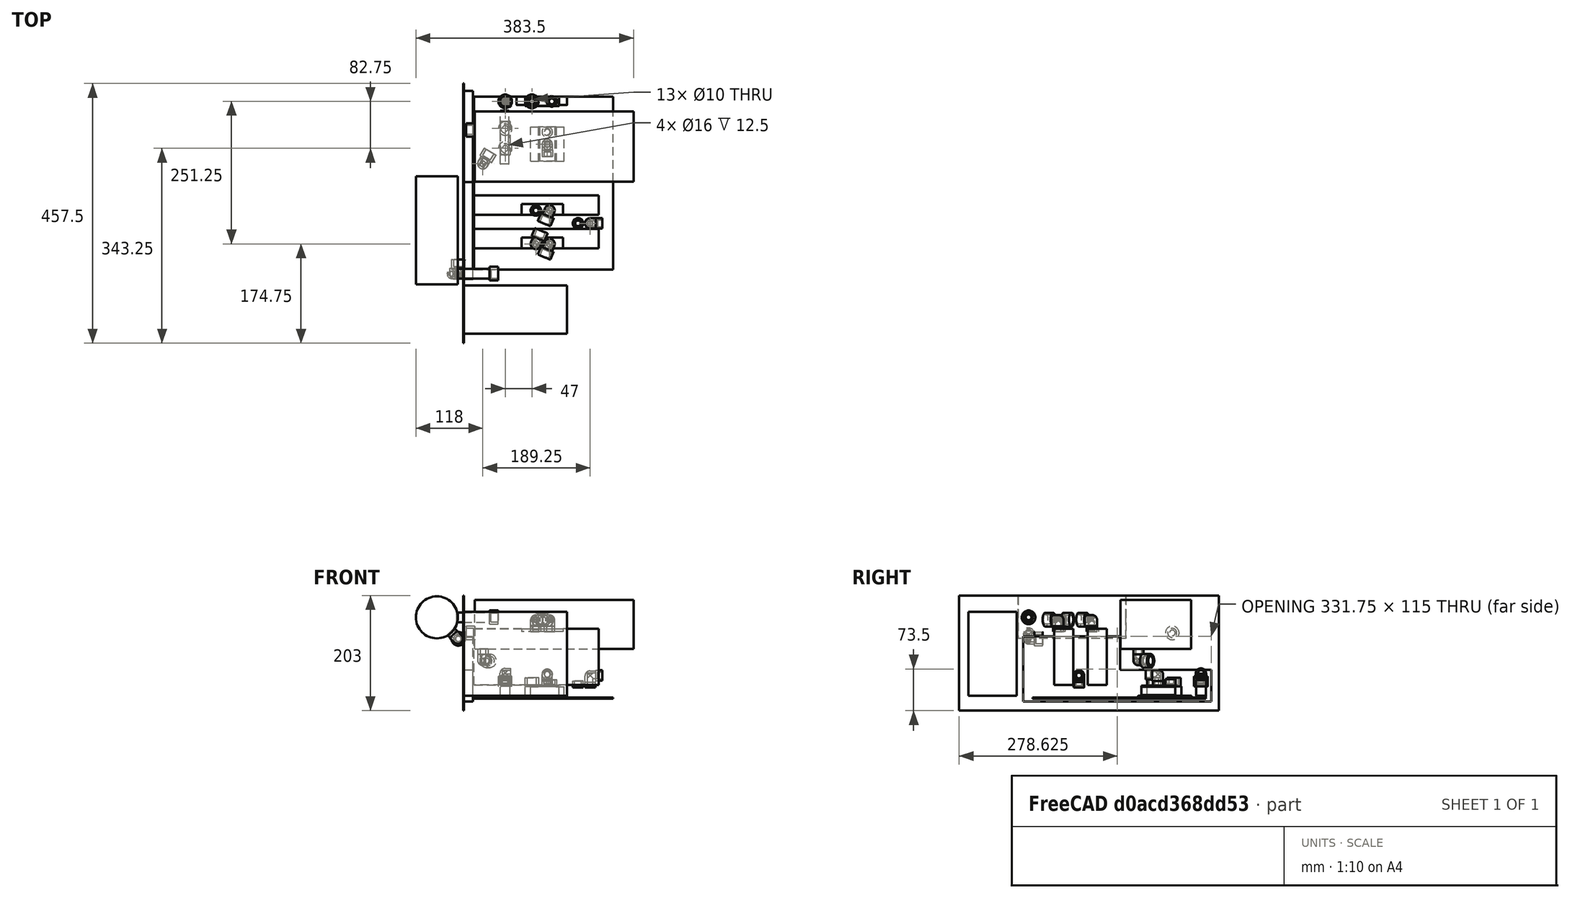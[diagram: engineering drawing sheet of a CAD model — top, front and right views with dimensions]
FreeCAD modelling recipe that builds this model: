
FCSTD DOCUMENT  (FreeCAD 0.18R16131 (Git))
Label: Model
License: All rights reserved
LicenseURL: http://en.wikipedia.org/wiki/All_rights_reserved
objects: TechDraw::DrawViewDimension×43, Part::Part2DObjectPython×40, Part::MultiFuse×29, Sketcher::SketchObject×22, Part::Cylinder×17, Part::Sweep×16, TechDraw::DrawViewPart×16, TechDraw::DrawViewAnnotation×13, Part::Cut×12, Part::Box×12, Part::Extrusion×11, Part::Fillet×7, App::DocumentObjectGroup×7, TechDraw::DrawSVGTemplate×6, TechDraw::DrawPage×6, Spreadsheet::Sheet×1
note: 166 computed .brp shape members not serialized (recipe doc carries the construction recipe); baked Part::Feature solids carry a one-line shape summary decoded from their .brp

FEATURE [Sketcher::SketchObject] Sketch  label="VRMs"
  expr: Constraints[15] = 51mm + References.LargeTubeOuterDiam
  expr: Constraints[7] = References.SmallTubeOuterDiam
  expr: Constraints[1] = References.LargeTubeOuterDiam
  sketch-geometry (11):
    g0: Circle CenterX=47 CenterY=0 CenterZ=0 NormalX=0 NormalY=0 NormalZ=1 AngleXU=0 Radius=8
    g1: Circle CenterX=0 CenterY=-47.7493 CenterZ=0 NormalX=0 NormalY=0 NormalZ=1 AngleXU=0 Radius=8
    g2: LineSegment [constr] StartX=0 StartY=-47.7493 StartZ=0 EndX=0 EndY=-82.7493 EndZ=0
    g3: Circle CenterX=0 CenterY=-82.7493 CenterZ=0 NormalX=0 NormalY=0 NormalZ=1 AngleXU=0 Radius=8
    g4: Circle CenterX=82 CenterY=0 CenterZ=0 NormalX=0 NormalY=0 NormalZ=1 AngleXU=0 Radius=6
    g5: LineSegment [constr] StartX=82 StartY=0 StartZ=0 EndX=74 EndY=0 EndZ=0
    g6: LineSegment [constr] StartX=74 StartY=0 StartZ=0 EndX=74 EndY=-54 EndZ=0
    g7: LineSegment StartX=82 StartY=0 StartZ=0 EndX=74 EndY=-54 EndZ=0
    g8: LineSegment [constr] StartX=47 StartY=0 StartZ=0 EndX=0 EndY=-47.7493 EndZ=0
    g9: LineSegment [constr] StartX=47 StartY=0 StartZ=0 EndX=82 EndY=0 EndZ=0
    g10: LineSegment StartX=47 StartY=0 StartZ=0 EndX=0 EndY=-82.7493 EndZ=0
  constraints (28):
    c: Distance(g-1,g0) = 47
    c: Diameter(g1) = 16
    c: Coincident(g2,g1)
    c: Vertical(g2)
    c: Equal(g0,g1)
    c: Equal(g1,g3)
    c: Coincident(g3,g2)
    c: Diameter(g4) = 12
    c: Horizontal(g5)
    c: Coincident(g4,g5)
    c: Vertical(g6)
    c: Coincident(g5,g6)
    c: Distance(g6) = 54
    c: Coincident(g7,g6)
    c: Coincident(g7,g4)
    c: Distance(g8) = 67
    c: Coincident(g1,g8)
    c: Coincident(g8,g0)
    c: Distance(g0,g4) = 35
    c: Distance(g5,g4) = 8
    c: PointOnObject(g4,g-1)
    c: PointOnObject(g0,g-1)
    c: PointOnObject(g1,g-2)
    c: Coincident(g9,g0)
    c: Coincident(g9,g4)
    c: Equal(g2,g9)
    c: Coincident(g10,g0)
    c: Coincident(g10,g3)
FEATURE [Part::Part2DObjectPython] Circle  label="VRM2-In"  # Draft 2D object (typed FeaturePython)
  FirstAngle = 0
  LastAngle = 0
  MakeFace = true
  Placement = pos=(0,-82.7493,0) rot=(0,0,1;0rad)
  Radius = 8
FEATURE [Part::Part2DObjectPython] Circle001  label="VRM2-Out"  # Draft 2D object (typed FeaturePython)
  FirstAngle = 0
  LastAngle = 0
  MakeFace = true
  Placement = pos=(0,-47.7493,0) rot=(0,0,1;0rad)
  Radius = 8
FEATURE [Part::Part2DObjectPython] Circle002  label="VRM1-Out"  # Draft 2D object (typed FeaturePython)
  FirstAngle = 0
  LastAngle = 0
  MakeFace = true
  Placement = pos=(47,0,0) rot=(0,0,1;0rad)
  Radius = 8
FEATURE [Part::Part2DObjectPython] Circle003  label="VRM1-In"  # Draft 2D object (typed FeaturePython)
  FirstAngle = 0
  LastAngle = 0
  MakeFace = true
  Placement = pos=(82,0,0) rot=(0,0,1;0rad)
  Radius = 6
FEATURE [Sketcher::SketchObject] Sketch001004  label="CPU-Sketch"
  Placement = pos=(0,0,2.5) rot=(0,0,1;0rad)
  expr: Constraints[10] = References.SmallPlugDiam
  expr: Constraints[14] = References.TurnCornLowDiam
  expr: Constraints[7] = References.SmallTubeOuterDiam
  sketch-geometry (7):
    g0: LineSegment [constr] StartX=0 StartY=0 StartZ=0 EndX=74 EndY=0 EndZ=0
    g1: LineSegment [constr] StartX=74 StartY=0 StartZ=0 EndX=74 EndY=-54 EndZ=0
    g2: Circle CenterX=74 CenterY=-54 CenterZ=0 NormalX=0 NormalY=0 NormalZ=1 AngleXU=0 Radius=6
    g3: LineSegment [constr] StartX=74 StartY=-44.75 StartZ=0 EndX=74 EndY=-84.75 EndZ=0
    g4: Circle [constr] CenterX=74 CenterY=-54 CenterZ=0 NormalX=0 NormalY=0 NormalZ=1 AngleXU=0 Radius=9.25
    g5: Circle [constr] CenterX=74 CenterY=-75.75 CenterZ=0 NormalX=0 NormalY=0 NormalZ=1 AngleXU=0 Radius=9
    g6: Circle CenterX=74 CenterY=-75.75 CenterZ=0 NormalX=0 NormalY=0 NormalZ=1 AngleXU=0 Radius=6
  constraints (19):
    c: Distance(g1) = 54
    c: Vertical(g1)
    c: Coincident(g0,g1)
    c: Coincident(g0,g-1)
    c: Horizontal(g0)
    c: Distance(g0) = 74
    c: Coincident(g2,g1)
    c: Diameter(g2) = 12
    c: Vertical(g3)
    c: Coincident(g4,g1)
    c: Diameter(g4) = 18.5
    c: PointOnObject(g3,g4)
    c: PointOnObject(g1,g3)
    c: Distance(g3) = 40
    c: Diameter(g5) = 18
    c: PointOnObject(g5,g3)
    c: PointOnObject(g3,g5)
    c: Coincident(g6,g5)
    c: Equal(g6,g2)
FEATURE [TechDraw::DrawSVGTemplate] Template001
  EditableTexts = Designed_by_Name=Christoph <owner>; Drawing_number=1; FC-Date=Date; FC-SC=1:1; FC-SH=2; FC-Title=PC Water Cooling; Subtitle=CPU - VRM -Tube; Weight=Weight
  Height = 210
  Orientation = 1
  Width = 297
FEATURE [TechDraw::DrawViewAnnotation] Annotation002
  Font = osifont
  LineSpace = 80
  LockPosition = false
  MaxWidth = -1
  Rotation = 0
  ScaleType = 0
  Text = Unbend
  TextSize = 8
  TextStyle = 0
  X = 136.406
  Y = 152.003
FEATURE [TechDraw::DrawViewAnnotation] Annotation003
  Font = osifont
  LineSpace = 80
  LockPosition = false
  MaxWidth = -1
  Rotation = 0
  ScaleType = 0
  Text = Bend
  TextSize = 8
  TextStyle = 0
  X = 108.764
  Y = 89.6129
FEATURE [Sketcher::SketchObject] Sketch001005004  label="GPUs-Base-Sketch"
  expr: Constraints[9] = 68mm + References.SmallPlugHeight
  sketch-geometry (9):
    g0: LineSegment StartX=-55 StartY=-165.75 StartZ=0 EndX=165 EndY=-165.75 EndZ=0
    g1: LineSegment StartX=165 StartY=-165.75 StartZ=0 EndX=165 EndY=-199.75 EndZ=0
    g2: LineSegment StartX=165 StartY=-199.75 StartZ=0 EndX=-55 EndY=-199.75 EndZ=0
    g3: LineSegment StartX=-55 StartY=-199.75 StartZ=0 EndX=-55 EndY=-165.75 EndZ=0
    g4: LineSegment [constr] StartX=74 StartY=-85.75 StartZ=0 EndX=74 EndY=-165.75 EndZ=0
    g5: LineSegment StartX=-55 StartY=-224.75 StartZ=0 EndX=165 EndY=-224.75 EndZ=0
    g6: LineSegment StartX=165 StartY=-258.75 StartZ=0 EndX=-55 EndY=-258.75 EndZ=0
    g7: LineSegment StartX=165 StartY=-224.75 StartZ=0 EndX=165 EndY=-258.75 EndZ=0
    g8: LineSegment StartX=-55 StartY=-258.75 StartZ=0 EndX=-55 EndY=-224.75 EndZ=0
  constraints (28):
    c: DistanceX(g-2,g4) = 74
    c: DistanceY(g-1,g4) = -85.75
    c: Coincident(g1,g2)
    c: Coincident(g2,g3)
    c: Coincident(g3,g0)
    c: Horizontal(g0)
    c: Horizontal(g2)
    c: Vertical(g1)
    c: Vertical(g3)
    c: Distance(g4) = 80
    c: Vertical(g4)
    c: PointOnObject(g4,g0)
    c: Distance(g0) = 220
    c: DistanceX(g-2,g0) = -55
    c: Distance(g1) = 34
    c: Coincident(g5,g7)
    c: Coincident(g7,g6)
    c: Coincident(g6,g8)
    c: Coincident(g8,g5)
    c: Horizontal(g5)
    c: Horizontal(g6)
    c: Vertical(g7)
    c: Vertical(g8)
    c: Equal(g0,g5) = 220
    c: Equal(g1,g7) = 35
    c: PointOnObject(g5,g3)
    c: Distance(g2,g5) = 25
    c: Coincident(g1,g0)
FEATURE [Sketcher::SketchObject] Sketch001005005  label="Chipset-Sketch"
  Placement = pos=(0,0,-1.5) rot=(0,0,1;0rad)
  sketch-geometry (4):
    g0: Circle CenterX=149.75 CenterY=-215 CenterZ=0 NormalX=0 NormalY=0 NormalZ=1 AngleXU=0 Radius=6
    g1: LineSegment [constr] StartX=0 StartY=-215 StartZ=0 EndX=149.75 EndY=-215 EndZ=0
    g2: LineSegment [constr] StartX=149.75 StartY=0 StartZ=0 EndX=149.75 EndY=-215 EndZ=0
    g3: Circle CenterX=128.25 CenterY=-215 CenterZ=0 NormalX=0 NormalY=0 NormalZ=1 AngleXU=0 Radius=6
  constraints (12):
    c: Diameter(g0) = 12
    c: Coincident(g1,g0)
    c: PointOnObject(g1,g-2)
    c: Horizontal(g1)
    c: Vertical(g2)
    c: PointOnObject(g2,g-1)
    c: Coincident(g2,g0)
    c: Distance(g2) = 215
    c: Distance(g1) = 149.75
    c: Equal(g0,g3)
    c: PointOnObject(g3,g1)
    c: Distance(g0,g3) = 21.5
FEATURE [Part::Part2DObjectPython] Circle009  label="CPU-In-Turned"  # Draft 2D object (typed FeaturePython)
  FirstAngle = 0
  LastAngle = 0
  MakeFace = true
  Placement = pos=(74,-88.75,16) rot=(1,0,0;1.5708rad)
  Radius = 6
  expr: Placement.Base.y = -85.75mm - References.SmallPlugOffset
  expr: Placement.Base.z = 1.5mm + References.TurnCornUpZOffset + References.SmallPlugOffset
FEATURE [Part::Part2DObjectPython] Circle010  label="Chipset-In"  # Draft 2D object (typed FeaturePython)
  FirstAngle = 0
  LastAngle = 0
  MakeFace = true
  Placement = pos=(128.25,-215,-1.5) rot=(0,0,1;0rad)
  Radius = 6
FEATURE [Part::Part2DObjectPython] Circle011  label="Chipset-Out"  # Draft 2D object (typed FeaturePython)
  FirstAngle = 0
  LastAngle = 0
  MakeFace = true
  Placement = pos=(149.75,-215,-1.5) rot=(0,0,1;0rad)
  Radius = 6
FEATURE [Sketcher::SketchObject] Sketch001005010  label="Chipset-VRM-Tube-Path3"
  Placement = pos=(0,0,23.5) rot=(0,0,1;0rad)
  expr: Constraints[27] = Constraints.Bend * pi / 4
  expr: Constraints.Bend = 43.5 + 12 / 2
  sketch-geometry (12):
    g0: GeomPoint X=74 Y=-88.75 Z=0
    g1: LineSegment [constr] StartX=0 StartY=-88.75 StartZ=0 EndX=74 EndY=-88.75 EndZ=0
    g2: LineSegment [constr] StartX=74 StartY=-88.75 StartZ=0 EndX=74 EndY=0 EndZ=0
    g3: LineSegment StartX=74 StartY=-88.75 StartZ=0 EndX=74 EndY=-131 EndZ=0
    g4: LineSegment StartX=183 StartY=-155.75 StartZ=0 EndX=98.75 EndY=-155.75 EndZ=0
    g5: ArcOfCircle CenterX=98.75 CenterY=-131 CenterZ=0 NormalX=0 NormalY=0 NormalZ=1 AngleXU=0 Radius=24.75 StartAngle=3.14159 EndAngle=4.71239
    g6: LineSegment [constr] StartX=183 StartY=0 StartZ=0 EndX=183 EndY=-155.75 EndZ=0
    g7: LineSegment [constr] StartX=183 StartY=-155.75 StartZ=0 EndX=0 EndY=-155.75 EndZ=0
    g8: LineSegment StartX=98.75 StartY=-135.75 StartZ=0 EndX=183 EndY=-135.75 EndZ=0
    g9: LineSegment StartX=183 StartY=-135.75 StartZ=0 EndX=221.877 EndY=-135.75 EndZ=0
    g10: LineSegment StartX=221.877 StartY=-135.75 StartZ=0 EndX=264.127 EndY=-135.75 EndZ=0
    g11: LineSegment [constr] StartX=98.75 StartY=-135.75 StartZ=0 EndX=98.75 EndY=-155.75 EndZ=0
  constraints (34):
    c: Coincident(g1,g0)
    c: Coincident(g1,g2)
    c: Horizontal(g1)
    c: Vertical(g2)
    c: PointOnObject(g1,g-2)
    c: PointOnObject(g2,g-1)
    c: Distance(g1) = 74
    c: Distance(g2) = 88.75
    c: Tangent(g5,g3) = -1.5708
    c: Tangent(g5,g4) = 1.5708
    c: Horizontal(g4)
    c: Vertical(g3)
    c: Coincident(g3,g0)
    c: Diameter(g5) = 49.5  'Bend'
    c: Vertical(g6)
    c: Horizontal(g7)
    c: Coincident(g4,g6)
    c: Coincident(g4,g7)
    c: PointOnObject(g6,g-1)
    c: PointOnObject(g7,g-2)
    c: Distance(g6) = 155.75
    c: Distance(g7) = 183
    c: Horizontal(g8)
    c: Horizontal(g9)
    c: Horizontal(g10)
    c: Coincident(g8,g9)
    c: Coincident(g9,g10)
    c: Distance(g9) = 38.8772
    c: Coincident(g11,g4)
    c: Coincident(g11,g8)
    c: Equal(g3,g10)
    c: Vertical(g11)
    c: PointOnObject(g8,g6)
    c: Distance(g11) = 20
FEATURE [Sketcher::SketchObject] Sketch001005011  label="Chipset-VRM-Tube-Path1"
  Placement = pos=(0,0,19.5) rot=(0,0,1;0rad)
  sketch-geometry (4):
    g0: GeomPoint X=162.75 Y=-215 Z=0
    g1: LineSegment [constr] StartX=162.75 StartY=-215 StartZ=0 EndX=0 EndY=-215 EndZ=0
    g2: LineSegment [constr] StartX=162.75 StartY=0 StartZ=0 EndX=162.75 EndY=-215 EndZ=0
    g3: LineSegment StartX=162.75 StartY=-215 StartZ=0 EndX=182.75 EndY=-215 EndZ=0
  constraints (11):
    c: Coincident(g0,g1)
    c: Coincident(g0,g2)
    c: PointOnObject(g1,g-2)
    c: Horizontal(g1)
    c: PointOnObject(g2,g-1)
    c: Vertical(g2)
    c: Distance(g2) = 215
    c: Distance(g1) = 162.75
    c: Horizontal(g3)
    c: Coincident(g3,g0)
    c: Distance(g3) = 20
FEATURE [Part::Part2DObjectPython] Line001  label="Chipset-CPU-Con"  # Draft 2D object (typed FeaturePython)
  ChamferSize = 0
  Closed = false
  End = (182.75,-215,16.5)
  FilletRadius = 0
  Length = 59.3264
  MakeFace = true
  Placement = pos=(183,-155.75,23.5) rot=(-0.578974,-0.576537,0.576537;2.09196rad)
  Points = (2) [(0,4,0),(-59.2505,7,2.84217e-14)]
  Start = (183,-155.75,19.5)
  Subdivisions = 0
  expr: End.z = -1.5mm - References.SmallPlugOffset + References.TurnCornZOffset
  expr: Start.z = 1.5mm - References.SmallPlugOffset + References.TurnCornZOffset
FEATURE [Part::Extrusion] Extrude010  label="Chipset-CPU-Plane"
  Base = -> Line001
  Dir = (-0.999991,0.00421937,-1e-16)
  DirMode = 2
  FaceMakerClass = Part::FaceMakerBullseye
  LengthFwd = 40
  LengthRev = 0
  Reversed = true
  Solid = false
  Symmetric = false
FEATURE [Sketcher::SketchObject] Sketch001005012  label="Chipset-VRM-Tube-Path2"
  ExternalGeometry = -> [Extrude010]
  MapMode = 5
  Placement = pos=(-0.00582736,-1.38108,27.2769) rot=(1,-3e-06,0.000107;3.19218rad)
  Support = -> [Extrude010]
  expr: Constraints[16] = Constraints.Bend * pi / 4
  expr: Constraints.Bend = 43.5 + 12 / 2
  sketch-geometry (7):
    g0: ArcOfCircle CenterX=182.86 CenterY=189.141 CenterZ=0 NormalX=0 NormalY=0 NormalZ=1 AngleXU=0 Radius=24.75 StartAngle=0 EndAngle=1.57501
    g1: ArcOfCircle CenterX=182.902 CenterY=179.273 CenterZ=0 NormalX=0 NormalY=0 NormalZ=1 AngleXU=0 Radius=24.7084 StartAngle=4.7166 EndAngle=6.28319
    g2: LineSegment StartX=207.61 StartY=189.141 StartZ=0 EndX=207.61 EndY=179.273 EndZ=0
    g3: LineSegment [constr] StartX=207.61 StartY=184.207 StartZ=0 EndX=227.61 EndY=184.207 EndZ=0
    g4: LineSegment StartX=227.61 StartY=228.018 StartZ=0 EndX=227.61 EndY=189.141 EndZ=0
    g5: LineSegment StartX=227.61 StartY=179.273 StartZ=0 EndX=227.61 EndY=140.396 EndZ=0
    g6: LineSegment StartX=227.61 StartY=189.141 StartZ=0 EndX=227.61 EndY=179.273 EndZ=0
  constraints (18):
    c: Vertical(g2)
    c: Tangent(g2,g0) = 1.5708
    c: Tangent(g2,g1) = 1.5708
    c: Tangent(g1,g-4) = -1.5708
    c: Tangent(g0,g-3) = 1.5708
    c: Diameter(g0) = 49.5  'Bend'
    c: Vertical(g6)
    c: Vertical(g4)
    c: Vertical(g5)
    c: Horizontal(g3)
    c: Symmetric(g2,g2,g3)
    c: Symmetric(g6,g6,g3)
    c: Equal(g6,g2)
    c: Coincident(g6,g5)
    c: Coincident(g4,g6)
    c: Equal(g5,g4)
    c: Distance(g5) = 38.8772
    c: Distance(g3) = 20
FEATURE [Part::Part2DObjectPython] Circle015  label="Chipset-Corn-Out"  # Draft 2D object (typed FeaturePython)
  FirstAngle = 0
  LastAngle = 0
  MakeFace = true
  Placement = pos=(162.75,-215,16.5) rot=(-0.578974,-0.576537,0.576537;2.09197rad)
  Radius = 6
  expr: Placement.Base.z = -1.5mm - References.SmallPlugOffset + References.TurnCornZOffset
FEATURE [Part::Sweep] Sweep005  label="Chipset-CPU-Tube-1"
  Frenet = false
  Sections = -> [Circle015]
  Solid = false
  Spine = -> Sketch001005011 [Edge1]
  Transition = 1
FEATURE [Part::Part2DObjectPython] Circle016  label="Chipset-CPU-Intermediate-1"  # Draft 2D object (typed FeaturePython)
  FirstAngle = 0
  LastAngle = 0
  MakeFace = true
  Placement = pos=(182.75,-215,16.5) rot=(-0.578974,-0.576537,0.576537;2.09197rad)
  Radius = 6
  expr: Placement.Base.z = -1.5mm + References.TurnCornZOffset - References.SmallPlugOffset
FEATURE [Part::Part2DObjectPython] Circle017  label="Chipset-CPU-Intermediate-2"  # Draft 2D object (typed FeaturePython)
  FirstAngle = 0
  LastAngle = 0
  MakeFace = true
  Placement = pos=(183,-155.75,19.5) rot=(-0.578974,-0.576537,0.576537;2.09197rad)
  Radius = 6
  expr: Placement.Base.z = 1.5mm - References.SmallPlugOffset + References.TurnCornZOffset
FEATURE [Part::Sweep] Sweep006  label="Chipset-CPU-Tube-2"
  Frenet = false
  Sections = -> [Circle016]
  Solid = false
  Spine = -> Sketch001005012 [Edge3,Edge2,Edge1]
  Transition = 1
FEATURE [Part::Sweep] Sweep007  label="Chipset-CPU-Tube-3"
  Frenet = false
  Sections = -> [Circle017]
  Solid = false
  Spine = -> Sketch001005010 [Edge3,Edge2,Edge1]
  Transition = 1
FEATURE [TechDraw::DrawSVGTemplate] Template002
  EditableTexts = Designed_by_Name=Christoph <owner>; Drawing_number=1; FC-Date=Date; FC-SC=1:1; FC-SH=3; FC-Title=PC Water Cooling; Subtitle=Chipset - CPU - Tube; Weight=Weight
  Height = 210
  Orientation = 1
  Width = 297
FEATURE [TechDraw::DrawViewPart] View004  label="Top"
  CoarseView = false
  Direction = (0,0,1)
  Focus = 100
  HardHidden = false
  IsoCount = 0
  IsoHidden = false
  IsoVisible = false
  LockPosition = false
  Perspective = false
  Rotation = 90
  ScaleType = 0
  SeamHidden = false
  SeamVisible = false
  SmoothHidden = false
  SmoothVisible = false
  Source = -> [Sweep005,Sweep006,Sweep007]
  X = 84.2384
  Y = 93.0457
FEATURE [TechDraw::DrawViewPart] View005  label="Side"
  CoarseView = false
  Direction = (0,1,0)
  Focus = 100
  HardHidden = false
  IsoCount = 0
  IsoHidden = false
  IsoVisible = false
  LockPosition = false
  Perspective = false
  Rotation = 0
  ScaleType = 0
  SeamHidden = false
  SeamVisible = false
  SmoothHidden = false
  SmoothVisible = false
  Source = -> [Sweep005,Sweep006,Sweep007]
  X = 193.805
  Y = 79.086
FEATURE [TechDraw::DrawViewDimension] Dimension022
  Arbitrary = false
  FormatSpec = %.2f
  LockPosition = false
  MeasureType = 1
  OverTolerance = 0
  References2D = -> [View005]
  Rotation = 0
  ScaleType = 0
  Type = 2
  UnderTolerance = 0
  X = -27.489
  Y = 18.168
FEATURE [Part::Part2DObjectPython] Circle018  label="Chipset-CPU-Unbend-2-Start"  # Draft 2D object (typed FeaturePython)
  FirstAngle = 0
  LastAngle = 0
  MakeFace = true
  Placement = pos=(227.604,-229.096,18.6236) rot=(-1,0,0;1.5708rad)
  Radius = 6
FEATURE [Part::Sweep] Sweep008  label="Chipset-CPU-Unbend-2"
  Frenet = false
  Sections = -> [Circle018]
  Solid = false
  Spine = -> Sketch001005012 [Edge4,Edge5,Edge6]
  Transition = 1
FEATURE [Part::Part2DObjectPython] Circle019  label="Chipset-CPU-Unbend-3-Start"  # Draft 2D object (typed FeaturePython)
  FirstAngle = 0
  LastAngle = 0
  MakeFace = true
  Placement = pos=(114.75,-135.75,23.5) rot=(0.57735,0.57735,0.57735;2.0944rad)
  Radius = 6
FEATURE [Part::Sweep] Sweep009  label="Chipset-CPU-Unbend-3"
  Frenet = false
  Sections = -> [Circle019]
  Solid = false
  Spine = -> Sketch001005010 [Edge4,Edge5,Edge6]
  Transition = 1
FEATURE [TechDraw::DrawViewPart] View006  label="Unbend1"
  CoarseView = false
  Direction = (0,1,0)
  Focus = 100
  HardHidden = false
  IsoCount = 0
  IsoHidden = false
  IsoVisible = false
  LockPosition = false
  Perspective = false
  Rotation = 0
  ScaleType = 0
  SeamHidden = false
  SeamVisible = false
  SmoothHidden = false
  SmoothVisible = false
  Source = -> [Sweep005]
  X = 272.886
  Y = 190.725
FEATURE [TechDraw::DrawViewPart] View007  label="Unbend2"
  CoarseView = false
  Direction = (1,0,0)
  Focus = 100
  HardHidden = false
  IsoCount = 0
  IsoHidden = false
  IsoVisible = false
  LockPosition = false
  Perspective = false
  Rotation = 0
  ScaleType = 0
  SeamHidden = false
  SeamVisible = false
  SmoothHidden = false
  SmoothVisible = false
  Source = -> [Sweep008]
  X = 219.254
  Y = 187.598
FEATURE [TechDraw::DrawViewPart] View008  label="Unbend3"
  CoarseView = false
  Direction = (0,1,0)
  Focus = 100
  HardHidden = false
  IsoCount = 0
  IsoHidden = false
  IsoVisible = false
  LockPosition = false
  Perspective = false
  Rotation = 0
  ScaleType = 0
  SeamHidden = false
  SeamVisible = false
  SmoothHidden = false
  SmoothVisible = false
  Source = -> [Sweep009]
  X = 93.7486
  Y = 184.77
FEATURE [TechDraw::DrawViewDimension] Dimension027
  Arbitrary = false
  FormatSpec = %.2f
  LockPosition = false
  MeasureType = 1
  OverTolerance = 0
  References2D = -> [View008]
  Rotation = 0
  ScaleType = 0
  Type = 1
  UnderTolerance = 0
  X = 0.425571
  Y = -9.8662
FEATURE [TechDraw::DrawViewDimension] Dimension028
  Arbitrary = false
  FormatSpec = %.2f
  LockPosition = false
  MeasureType = 1
  OverTolerance = 0
  References2D = -> [View007]
  Rotation = 0
  ScaleType = 0
  Type = 0
  UnderTolerance = 0
  X = 3.46058
  Y = -10.0125
FEATURE [TechDraw::DrawViewDimension] Dimension029
  Arbitrary = false
  FormatSpec = %.2f
  LockPosition = false
  MeasureType = 1
  OverTolerance = 0
  References2D = -> [View006]
  Rotation = 0
  ScaleType = 0
  Type = 1
  UnderTolerance = 0
  X = -0.341951
  Y = -24.0175
FEATURE [TechDraw::DrawViewAnnotation] Annotation004
  Font = osifont
  LineSpace = 80
  LockPosition = false
  MaxWidth = -1
  Rotation = 0
  ScaleType = 0
  Text = Top View
  TextSize = 8
  TextStyle = 0
  X = 49.8933
  Y = 147.612
FEATURE [TechDraw::DrawViewAnnotation] Annotation005
  Font = osifont
  LineSpace = 80
  LockPosition = false
  MaxWidth = -1
  Rotation = 0
  ScaleType = 0
  Text = Side View
  TextSize = 8
  TextStyle = 0
  X = 213.956
  Y = 102.638
FEATURE [TechDraw::DrawViewAnnotation] Annotation006
  Font = osifont
  LineSpace = 80
  LockPosition = false
  MaxWidth = -1
  Rotation = 0
  ScaleType = 0
  Text = Unbend
  TextSize = 8
  TextStyle = 0
  X = 232.772
  Y = 161.972
FEATURE [Spreadsheet::Sheet] Spreadsheet  label="References"
  cells = B2=Small Plug; C2=Large Plug; D2=Extension; A3=Diameter; B3(SmallPlugDiam)==18.5mm; C3(LargePlugDiam)==24mm; D3(ExtensionDiamater)==17mm; A4=Height; B4(SmallPlugHeight)==12mm; C4(LargePlugHeight)==15mm; D4(ExtensionHeight)==7mm; A5=Tube Offset; B5(SmallPlugOffset)==3mm; C5(LargePlugOffset)==LargePlugHeight - 12.5mm; B7=SmallTube; C7=LargeTube; A8=Inner Diameter; B8(SmallTubeInnerDiam)==10mm; C8(LargeTubeInnerDiam)==13mm; A9=Outer Diameter; B9(SmallTubeOuterDiam)==12mm; C9(LargeTubeOuterDiam)==16mm; A10=Radius; B10(SmallTubeBendDiam)==43.5mm + SmallTubeOuterDiam; C10(LargeTubeBendDiam)==45mm + LargeTubeOuterDiam; A11=Straight Length; B11(SmallTubeStraightLen)==10mm; C11(LargTubeStraightLen)==20mm; B13=TurnableCorner; C13=Corner; A14=Height Offset; B14(TurnCornZOffset)==TurnCornLowHeight + TurnCornUpZOffset; C14(CornZOffset)==TurnCornUpZOffset; A15=Front Offset; B15(TurnCornXOffset)==TurnCornUpLen - TurnCornLowDiam / 2; C15(CornXOffset)==TurnCornXOffset; A16=Lower Diam; B16(TurnCornLowDiam)==18mm; C16==0mm; A17=Upper Width; B17(TurnCornUpWid)==18mm; C17(CornWid)==TurnCornUpWid; A18=Upper Length; B18(TurnCornUpLen)==19mm; C18(CornLen)==TurnCornUpLen; A19=Upper Height Offset; B19(TurnCornUpZOffset)==TurnCornUpHeight - 2mm - SmallTubeOuterDiam / 2; C19==TurnCornUpZOffset; A20=Lower Height; B20(TurnCornLowHeight)==9.5mm; C20==0mm; A21=Upper Height; B21(TurnCornUpHeight)==19.5mm; C21(CornHeight)==TurnCornUpHeight; A24=Unbend Tube Offset; B24(UnbendOffset)==20mm
FEATURE [Part::Part2DObjectPython] Line004  label="VRM-VRM-Con"  # Draft 2D object (typed FeaturePython)
  ChamferSize = 0
  Closed = false
  End = (0,-47.7493,0)
  FilletRadius = 0
  Length = 67
  MakeFace = true
  Points = (2) [(47,0,0),(0,-47.7493,0)]
  Start = (47,0,0)
  Subdivisions = 0
FEATURE [Part::Part2DObjectPython] Circle022  label="CPU-In"  # Draft 2D object (typed FeaturePython)
  FirstAngle = 0
  LastAngle = 0
  MakeFace = true
  Placement = pos=(74,-75.75,2.5) rot=(0,0,1;0rad)
  Radius = 6
FEATURE [Part::Part2DObjectPython] Circle023  label="CPU-Out"  # Draft 2D object (typed FeaturePython)
  FirstAngle = 0
  LastAngle = 0
  MakeFace = true
  Placement = pos=(74,-54,1.5) rot=(0,0,1;0rad)
  Radius = 6
FEATURE [Part::Part2DObjectPython] Line005  label="CPU-VRM-Con"  # Draft 2D object (typed FeaturePython)
  ChamferSize = 0
  Closed = false
  End = (74,-54,0)
  FilletRadius = 0
  Length = 54.5894
  MakeFace = true
  Points = (2) [(82,0,0),(74,-54,0)]
  Start = (82,0,0)
  Subdivisions = 0
FEATURE [Part::Extrusion] Extrude011  label="CPU-VRM-Plane"
  Base = -> Line005
  Dir = (0,0,1)
  DirMode = 2
  FaceMakerClass = Part::FaceMakerBullseye
  LengthFwd = 60
  LengthRev = 0
  Solid = false
  Symmetric = false
FEATURE [Sketcher::SketchObject] Sketch001005014  label="CPU-VRM-Sketch"
  ExternalGeometry = -> [Extrude011]
  MapMode = 5
  Placement = pos=(80.2389,-11.8872,0) rot=(0.633886,0.546895,0.546895;2.01166rad)
  Support = -> [Extrude011]
  expr: Constraints[12] = References.UnbendOffset
  expr: Constraints[2] = References.SmallTubeStraightLen
  sketch-geometry (9):
    g0: LineSegment StartX=-42.5724 StartY=2 StartZ=0 EndX=-42.5724 EndY=12 EndZ=0
    g1: ArcOfCircle CenterX=-15.2824 CenterY=12 CenterZ=0 NormalX=0 NormalY=0 NormalZ=1 AngleXU=0 Radius=27.29 StartAngle=1.5708 EndAngle=3.14159
    g2: LineSegment StartX=-15.2824 StartY=39.29 StartZ=0 EndX=-15.273 EndY=39.29 EndZ=0
    g3: ArcOfCircle CenterX=-15.273 CenterY=12 CenterZ=0 NormalX=0 NormalY=0 NormalZ=1 AngleXU=0 Radius=27.29 StartAngle=0 EndAngle=1.5708
    g4: LineSegment StartX=-15.273 StartY=59.29 StartZ=0 EndX=-15.2824 EndY=59.29 EndZ=0
    g5: LineSegment StartX=-15.273 StartY=59.29 StartZ=0 EndX=39.0705 EndY=59.29 EndZ=0
    g6: LineSegment StartX=-15.2824 StartY=59.29 StartZ=0 EndX=-68.1259 EndY=59.29 EndZ=0
    g7: LineSegment [constr] StartX=-15.2777 StartY=59.29 StartZ=0 EndX=-15.2777 EndY=39.29 EndZ=0
    g8: LineSegment StartX=12.017 StartY=12 StartZ=0 EndX=12.017 EndY=0.5 EndZ=0
  constraints (25):
    c: Tangent(g0,g1) = 1.5708
    c: Tangent(g0,g-4) = -1.5708
    c: Distance(g0) = 10
    c: Tangent(g2,g1) = 1.5708
    c: Tangent(g3,g2) = 1.5708
    c: Horizontal(g2)
    c: Equal(g3,g1)
    c: Equal(g2,g4)
    c: Horizontal(g4)
    c: Symmetric(g4,g4,g7)
    c: Vertical(g7)
    c: Symmetric(g2,g2,g7)
    c: Distance(g7) = 20
    c: Distance(g5) = 54.3435
    c: Distance(g6) = 52.8435
    c: Coincident(g4,g6)
    c: Coincident(g5,g4)
    c: Horizontal(g5)
    c: Horizontal(g6)
    c: Distance(g0,g-4) = 2
    c: Vertical(g8)
    c: Distance(g8,g-3) = 0.5
    c: Tangent(g8,g3) = 1.5708
    c: PointOnObject(g8,g-3)
    c: Diameter(g1) = 54.58
FEATURE [Part::Part2DObjectPython] Circle024  label="CPU-VRM-Unbend-Start"  # Draft 2D object (typed FeaturePython)
  FirstAngle = 0
  LastAngle = 0
  MakeFace = true
  Placement = pos=(70.253,-79.2924,59.775) rot=(0.994616,-0.073275,-0.073275;1.5762rad)
  Radius = 6
FEATURE [Part::Sweep] Sweep  label="CPU-VRM-Unbend"
  Frenet = false
  Sections = -> [Circle024]
  Solid = false
  Spine = -> Sketch001005014 [Edge8,Edge7,Edge6]
  Transition = 1
FEATURE [TechDraw::DrawViewPart] View002  label="Unbend"
  CoarseView = false
  Direction = (0.54,-0.08,0)
  Focus = 100
  HardHidden = false
  IsoCount = 0
  IsoHidden = false
  IsoVisible = false
  LockPosition = false
  Perspective = false
  Rotation = 0
  ScaleType = 0
  SeamHidden = false
  SeamVisible = false
  SmoothHidden = false
  SmoothVisible = false
  Source = -> [Sweep]
  X = 138.605
  Y = 177.84
FEATURE [TechDraw::DrawViewDimension] Dimension035
  Arbitrary = false
  FormatSpec = %.2f
  LockPosition = false
  MeasureType = 1
  OverTolerance = 0
  References2D = -> [View002]
  Rotation = 0
  ScaleType = 0
  Type = 1
  UnderTolerance = 0
  X = -0.301104
  Y = -13.2265
FEATURE [Part::Sweep] Sweep014  label="CPU-VRM-Tube"
  Frenet = false
  Sections = -> [Circle023]
  Solid = false
  Spine = -> Sketch001005014 [Edge1,Edge2,Edge3,Edge4,Edge5]
  Transition = 1
FEATURE [TechDraw::DrawViewPart] View003  label="Side001"
  CoarseView = false
  Direction = (-54,8,0)
  Focus = 100
  HardHidden = false
  IsoCount = 0
  IsoHidden = false
  IsoVisible = false
  LockPosition = false
  Perspective = false
  Rotation = 0
  ScaleType = 0
  SeamHidden = false
  SeamVisible = false
  SmoothHidden = false
  SmoothVisible = false
  Source = -> [Sweep014]
  X = 88.8407
  Y = 48.4082
FEATURE [TechDraw::DrawViewDimension] Dimension047
  Arbitrary = false
  FormatSpec = %.2f
  LockPosition = false
  MeasureType = 1
  OverTolerance = 0
  References2D = -> [View004]
  Rotation = 0
  ScaleType = 0
  Type = 1
  UnderTolerance = 0
  X = -26.3419
  Y = -48.8146
FEATURE [TechDraw::DrawViewDimension] Dimension054
  Arbitrary = false
  FormatSpec = %.2f
  LockPosition = false
  MeasureType = 1
  OverTolerance = 0
  References2D = -> [View005]
  Rotation = 0
  ScaleType = 0
  Type = 2
  UnderTolerance = 0
  X = 77.308
  Y = 2.11203
FEATURE [TechDraw::DrawViewDimension] Dimension055
  Arbitrary = false
  FormatSpec = %.2f
  LockPosition = false
  MeasureType = 1
  OverTolerance = 0
  References2D = -> [View004]
  Rotation = 0
  ScaleType = 0
  Type = 2
  UnderTolerance = 0
  X = -11.4999
  Y = 24.5166
FEATURE [TechDraw::DrawViewDimension] Dimension056
  Arbitrary = false
  FormatSpec = %.2f
  LockPosition = false
  MeasureType = 1
  OverTolerance = 0
  References2D = -> [View004]
  Rotation = 0
  ScaleType = 0
  Type = 2
  UnderTolerance = 0
  X = -45.683
  Y = -30.4883
FEATURE [TechDraw::DrawViewDimension] Dimension057
  Arbitrary = false
  FormatSpec = %.2f
  LockPosition = false
  MeasureType = 1
  OverTolerance = 0
  References2D = -> [View004]
  Rotation = 0
  ScaleType = 0
  Type = 2
  UnderTolerance = 0
  X = 13.3488
  Y = 1.82286
FEATURE [TechDraw::DrawViewDimension] Dimension058
  Arbitrary = false
  FormatSpec = %.2f
  LockPosition = false
  MeasureType = 1
  OverTolerance = 0
  References2D = -> [View004]
  Rotation = 0
  ScaleType = 0
  Type = 1
  UnderTolerance = 0
  X = 43.1032
  Y = 56.7834
FEATURE [TechDraw::DrawViewDimension] Dimension059
  Arbitrary = false
  FormatSpec = %.2f
  LockPosition = false
  MeasureType = 1
  OverTolerance = 0
  References2D = -> [View004]
  Rotation = 0
  ScaleType = 0
  Type = 1
  UnderTolerance = 0
  X = -30.1279
  Y = -75.7031
FEATURE [TechDraw::DrawViewDimension] Dimension060
  Arbitrary = false
  FormatSpec = %.2f
  LockPosition = false
  MeasureType = 1
  OverTolerance = 0
  References2D = -> [View004]
  Rotation = 0
  ScaleType = 0
  Type = 1
  UnderTolerance = 0
  X = 30.2026
  Y = 32.8589
FEATURE [TechDraw::DrawViewDimension] Dimension061
  Arbitrary = false
  FormatSpec = %.2f
  LockPosition = false
  MeasureType = 1
  OverTolerance = 0
  References2D = -> [View004]
  Rotation = 0
  ScaleType = 0
  Type = 2
  UnderTolerance = 0
  X = -63.6273
  Y = 34.9692
FEATURE [TechDraw::DrawPage] Page002  label="Chipset-CPU-Tube-Drawing"
  KeepUpdated = true
  ProjectionType = 0
  Template = -> Template002
  Views = -> [View004,View005,Dimension022,View006,View007,View008,Dimension027,Dimension028,Dimension029,Annotation004,Annotation005,Annotation006,Dimension047,Dimension054,Dimension055,Dimension056,Dimension057,Dimension058,Dimension059,Dimension060,Dimension061]
FEATURE [Part::Extrusion] Extrude012  label="GPU-Base"
  Base = -> Sketch001005004
  Dir = (0,0,1)
  DirMode = 2
  FaceMakerClass = Part::FaceMakerBullseye
  LengthFwd = 99
  LengthRev = 0
  Solid = true
  Symmetric = false
FEATURE [Sketcher::SketchObject] Sketch001005015  label="GPU-Pocket-Sketch"
  ExternalGeometry = -> [Extrude012]
  MapMode = 45
  Placement = pos=(55,-212.25,99) rot=(0,0,1;1.5708rad)
  Support = -> [Extrude012]
  sketch-geometry (10):
    g0: LineSegment [constr] StartX=12.5 StartY=110 StartZ=0 EndX=12.5 EndY=26 EndZ=0
    g1: LineSegment StartX=12.5 StartY=26 StartZ=0 EndX=31.5 EndY=26 EndZ=0
    g2: LineSegment StartX=31.5 StartY=26 StartZ=0 EndX=31.5 EndY=-47 EndZ=0
    g3: LineSegment StartX=12.5 StartY=26 StartZ=0 EndX=12.5 EndY=-47 EndZ=0
    g4: LineSegment StartX=12.5 StartY=-47 StartZ=0 EndX=31.5 EndY=-47 EndZ=0
    g5: LineSegment [constr] StartX=-46.5 StartY=110 StartZ=0 EndX=-46.5 EndY=26 EndZ=0
    g6: LineSegment StartX=-46.5 StartY=26 StartZ=0 EndX=-27.5 EndY=26 EndZ=0
    g7: LineSegment StartX=-27.5 StartY=26 StartZ=0 EndX=-27.5 EndY=-47 EndZ=0
    g8: LineSegment StartX=-27.5 StartY=-47 StartZ=0 EndX=-46.5 EndY=-47 EndZ=0
    g9: LineSegment StartX=-46.5 StartY=-47 StartZ=0 EndX=-46.5 EndY=26 EndZ=0
  constraints (28):
    c: Coincident(g0,g1)
    c: Coincident(g1,g2)
    c: Vertical(g0)
    c: Horizontal(g1)
    c: Vertical(g2)
    c: Coincident(g0,g-3)
    c: Distance(g0) = 84
    c: Distance(g1) = 19
    c: Distance(g2) = 73
    c: Coincident(g4,g2)
    c: Coincident(g4,g3)
    c: Coincident(g0,g3)
    c: Horizontal(g4)
    c: Vertical(g3)
    c: Coincident(g6,g7)
    c: Coincident(g7,g8)
    c: Coincident(g8,g9)
    c: Coincident(g9,g6)
    c: Horizontal(g6)
    c: Horizontal(g8)
    c: Vertical(g7)
    c: Vertical(g9)
    c: Coincident(g6,g5)
    c: Coincident(g5,g-4)
    c: Vertical(g5)
    c: Equal(g6,g1)
    c: Equal(g5,g0)
    c: Equal(g2,g7)
FEATURE [Part::Extrusion] Extrude013  label="Con-Holes"
  Base = -> Sketch001005015
  Dir = (0,0,1)
  DirMode = 2
  FaceMakerClass = Part::FaceMakerBullseye
  LengthFwd = 5
  LengthRev = 0
  Reversed = true
  Solid = true
  Symmetric = false
FEATURE [Part::Cut] Cut002  label="GPUs"
  Base = -> Extrude012
  Tool = -> Extrude013
FEATURE [Sketcher::SketchObject] Sketch001005016  label="GPU-Sketch"
  ExternalGeometry = -> [Cut002]
  MapMode = 45
  Placement = pos=(65.5,-219.75,94) rot=(0,0,1;0rad)
  Support = -> [Cut002]
  expr: Constraints[32] = Constraints.Right
  expr: Constraints[17] = References.LargeTubeOuterDiam
  expr: Constraints[33] = Constraints.Left
  expr: Constraints[15] = References.SmallTubeOuterDiam
  expr: Constraints[0] = References.TurnCornLowDiam
  sketch-geometry (17):
    g0: Circle [constr] CenterX=12.5 CenterY=27.5 CenterZ=0 NormalX=0 NormalY=0 NormalZ=1 AngleXU=0 Radius=9
    g1: GeomPoint X=3.5 Y=27.5 Z=0
    g2: Circle [constr] CenterX=-11.5 CenterY=27.5 CenterZ=0 NormalX=0 NormalY=0 NormalZ=1 AngleXU=0 Radius=9
    g3: LineSegment [constr] StartX=-11.5 StartY=27.5 StartZ=0 EndX=12.5 EndY=27.5 EndZ=0
    g4: GeomPoint X=-2.5 Y=27.5 Z=0
    g5: LineSegment [constr] StartX=-11.5 StartY=39 StartZ=0 EndX=-11.5 EndY=36.5 EndZ=0
    g6: Circle CenterX=-11.5 CenterY=27.5 CenterZ=0 NormalX=0 NormalY=0 NormalZ=1 AngleXU=0 Radius=6
    g7: Circle CenterX=12.5 CenterY=27.5 CenterZ=0 NormalX=0 NormalY=0 NormalZ=1 AngleXU=0 Radius=8
    g8: Circle CenterX=-11.5 CenterY=-31.5 CenterZ=0 NormalX=0 NormalY=0 NormalZ=1 AngleXU=0 Radius=8
    g9: Circle [constr] CenterX=-11.5 CenterY=-31.5 CenterZ=0 NormalX=0 NormalY=0 NormalZ=1 AngleXU=0 Radius=9
    g10: Circle [constr] CenterX=12.5 CenterY=-31.5 CenterZ=0 NormalX=0 NormalY=0 NormalZ=1 AngleXU=0 Radius=9
    g11: Circle CenterX=12.5 CenterY=-31.5 CenterZ=0 NormalX=0 NormalY=0 NormalZ=1 AngleXU=0 Radius=8
    g12: LineSegment [constr] StartX=-11.5 StartY=-31.5 StartZ=0 EndX=12.5 EndY=-31.5 EndZ=0
    g13: GeomPoint X=-2.5 Y=-31.5 Z=0
    g14: GeomPoint X=3.5 Y=-31.5 Z=0
    g15: LineSegment [constr] StartX=-11.5 StartY=-20 StartZ=0 EndX=-11.5 EndY=-22.5 EndZ=0
    g16: LineSegment StartX=12.5 StartY=27.5 StartZ=0 EndX=-11.5 EndY=-31.5 EndZ=0
  constraints (40):
    c: Diameter(g0) = 18
    c: PointOnObject(g1,g0)
    c: Distance(g1,g-3) = 40  'Left'
    c: Equal(g2,g0)
    c: Coincident(g3,g0)
    c: Coincident(g2,g3)
    c: Horizontal(g3)
    c: PointOnObject(g4,g2)
    c: Distance(g4,g-5) = 39  'Right'
    c: PointOnObject(g4,g3)
    c: PointOnObject(g1,g3)
    c: Distance(g5) = 2.5
    c: Perpendicular(g5,g-6) = 1.5708
    c: PointOnObject(g5,g2)
    c: PointOnObject(g2,g5)
    c: Diameter(g6) = 12
    c: Coincident(g6,g2)
    c: Diameter(g7) = 16
    c: Coincident(g7,g0)
    c: Coincident(g9,g8)
    c: Coincident(g9,g12)
    c: Coincident(g11,g10)
    c: Coincident(g11,g12)
    c: Horizontal(g12)
    c: Equal(g9,g2)
    c: Equal(g8,g7)
    c: Equal(g11,g7)
    c: Equal(g10,g0)
    c: PointOnObject(g13,g12)
    c: PointOnObject(g13,g9)
    c: PointOnObject(g14,g10)
    c: PointOnObject(g14,g12)
    c: Distance(g13,g-8) = 39
    c: Distance(g14,g-4) = 40
    c: Perpendicular(g15,g-7) = 1.5708
    c: PointOnObject(g15,g9)
    c: PointOnObject(g8,g15)
    c: Equal(g15,g5)
    c: Coincident(g16,g7)
    c: Coincident(g16,g8)
FEATURE [Part::Part2DObjectPython] Circle025  label="GPU2-Out"  # Draft 2D object (typed FeaturePython)
  FirstAngle = 0
  LastAngle = 0
  MakeFace = true
  Placement = pos=(54,-192.25,97) rot=(0,0,1;0rad)
  Radius = 6
FEATURE [Part::Part2DObjectPython] Circle026  label="GPU1-Out"  # Draft 2D object (typed FeaturePython)
  FirstAngle = 0
  LastAngle = 0
  MakeFace = true
  Placement = pos=(54,-251.25,94) rot=(0,0,1;0rad)
  Radius = 8
FEATURE [Part::Part2DObjectPython] Circle027  label="GPU1-In"  # Draft 2D object (typed FeaturePython)
  FirstAngle = 0
  LastAngle = 0
  MakeFace = true
  Placement = pos=(78,-251.25,94) rot=(0,0,1;0rad)
  Radius = 8
FEATURE [Part::Part2DObjectPython] Circle028  label="GPU2-In"  # Draft 2D object (typed FeaturePython)
  FirstAngle = 0
  LastAngle = 0
  MakeFace = true
  Placement = pos=(78,-192.25,94) rot=(0,0,1;0rad)
  Radius = 8
FEATURE [Part::Part2DObjectPython] Line  label="CPU-Chipset-Con"  # Draft 2D object (typed FeaturePython)
  ChamferSize = 0
  Closed = false
  End = (128.25,-215,-1.5)
  FilletRadius = 0
  Length = 77.6571
  MakeFace = false
  Placement = pos=(64,-164,0) rot=(0,0,1;0rad)
  Points = (2) [(-10,-28.25,-1.5),(64.25,-51,-1.5)]
  Start = (54,-192.25,-1.5)
  Subdivisions = 0
  Support = -> [Circle025]
FEATURE [Part::Extrusion] Extrude014  label="GPU-Chipset-Plane"
  Base = -> Line
  Dir = (0,0,1)
  DirMode = 2
  FaceMakerClass = Part::FaceMakerBullseye
  LengthFwd = 120
  LengthRev = 0
  Solid = false
  Symmetric = false
FEATURE [Sketcher::SketchObject] Sketch001005017  label="GPU-Chipset-Sketch"
  ExternalGeometry = -> [Extrude014]
  MapMode = 5
  Placement = pos=(-49.2151,-160.625,0) rot=(0.105309,0.703175,0.703175;2.93175rad)
  Support = -> [Extrude014]
  expr: Constraints[15] = References.SmallTubeBendDiam * pi / 4 + References.SmallTubeStraightLen
  expr: Constraints[9] = References.SmallTubeStraightLen
  expr: Constraints[14] = References.UnbendOffset
  expr: Constraints[10] = References.SmallTubeBendDiam
  expr: Constraints[16] = References.SmallTubeBendDiam * pi / 4 + Constraints.GPUZOffset + References.SmallTubeStraightLen
  sketch-geometry (9):
    g0: LineSegment StartX=-185.608 StartY=-1.5 StartZ=0 EndX=-185.608 EndY=107 EndZ=0
    g1: LineSegment StartX=-107.951 StartY=97 StartZ=0 EndX=-107.951 EndY=107 EndZ=0
    g2: ArcOfCircle CenterX=-135.701 CenterY=107 CenterZ=0 NormalX=0 NormalY=0 NormalZ=1 AngleXU=0 Radius=27.75 StartAngle=2e-16 EndAngle=1.5708
    g3: ArcOfCircle CenterX=-157.858 CenterY=107 CenterZ=0 NormalX=0 NormalY=0 NormalZ=1 AngleXU=0 Radius=27.75 StartAngle=1.5708 EndAngle=3.14159
    g4: LineSegment StartX=-135.701 StartY=134.75 StartZ=0 EndX=-157.858 EndY=134.75 EndZ=0
    g5: LineSegment [constr] StartX=-146.78 StartY=134.75 StartZ=0 EndX=-146.78 EndY=154.75 EndZ=0
    g6: LineSegment StartX=-135.701 StartY=154.75 StartZ=0 EndX=-82.1117 EndY=154.75 EndZ=0
    g7: LineSegment StartX=-157.858 StartY=154.75 StartZ=0 EndX=-309.948 EndY=154.75 EndZ=0
    g8: LineSegment StartX=-157.858 StartY=154.75 StartZ=0 EndX=-135.701 EndY=154.75 EndZ=0
  constraints (23):
    c: Tangent(g4,g2) = -1.5708
    c: Tangent(g2,g1) = -1.5708
    c: Tangent(g4,g3) = -1.5708
    c: Tangent(g3,g0) = 1.5708
    c: Tangent(g0,g-4) = -1.5708
    c: Tangent(g1,g-3) = -1.5708
    c: Horizontal(g4)
    c: Equal(g2,g3)
    c: Distance(g1,g-3) = 98.5  'GPUZOffset'
    c: Distance(g1) = 10
    c: Diameter(g2) = 55.5
    c: Symmetric(g6,g7,g5)
    c: Symmetric(g4,g4,g5)
    c: Vertical(g5)
    c: Distance(g5) = 20
    c: Distance(g6) = 53.5896
    c: Distance(g7) = 152.09
    c: Horizontal(g7)
    c: Horizontal(g6)
    c: Coincident(g8,g7)
    c: Coincident(g8,g6)
    c: Horizontal(g8)
    c: Equal(g8,g4)
FEATURE [Part::Part2DObjectPython] Circle029  label="GPU-Chipset-Unbend-Start"  # Draft 2D object (typed FeaturePython)
  FirstAngle = 0
  LastAngle = 0
  MakeFace = true
  Placement = pos=(29.2941,-184.68,151.75) rot=(-0.691105,-0.511065,0.511065;1.93213rad)
  Radius = 6
  expr: Radius = References.SmallTubeOuterDiam / 2
FEATURE [Part::Sweep] Sweep015  label="GPU-Chipset-Unbend"
  Frenet = false
  Sections = -> [Circle029]
  Solid = false
  Spine = -> Sketch001005017 [Edge8,Edge7,Edge6]
  Transition = 1
FEATURE [Part::Sweep] Sweep016  label="GPU-Chipset-Tube"
  Frenet = false
  Sections = -> [Circle025]
  Solid = false
  Spine = -> Sketch001005017 [Edge5,Edge4,Edge3,Edge2,Edge1]
  Transition = 1
FEATURE [Part::Cylinder] Cylinder019  label="LargePlugBase"
  Angle = 360
  AttacherType = Attacher::AttachEngine3D
  Height = 2.5
  Radius = 12
  expr: Height = References.LargePlugOffset
  expr: Radius = References.LargePlugDiam / 2
FEATURE [Part::Cylinder] Cylinder020  label="TC-Bottom"
  Angle = 360
  AttacherType = Attacher::AttachEngine3D
  Height = 9.5
  Radius = 9
  expr: Placement.Base.z = 0
FEATURE [Part::Cylinder] Cylinder021  label="TC-Bottom-Hole"
  Angle = 360
  AttacherType = Attacher::AttachEngine3D
  Height = 25
  Radius = 5
  expr: Radius = References003.SmallTubeInnerDiam / 2
FEATURE [Part::Cylinder] Cylinder022  label="TC-Top-Hole"
  Angle = 360
  AttacherType = Attacher::AttachEngine3D
  Height = 15
  Placement = pos=(-5,0,21) rot=(0,1,0;1.5708rad)
  Radius = 5
  expr: Placement.Base.x = References.TurnCornXOffset - 15mm
  expr: Placement.Base.z = References.TurnCornZOffset
  expr: Radius = References.SmallTubeInnerDiam / 2
FEATURE [Part::Box] Box007  label="TC-Top-Base"
  AttacherType = Attacher::AttachEngine3D
  Height = 19.5
  Length = 19
  Placement = pos=(-9,-9,9.5) rot=(0,0,1;0rad)
  Width = 18
  expr: Placement.Base.z = References001.TurnCornLowHeight
  expr: Placement.Base.y = -References001.TurnCornLowDiam / 2
  expr: Placement.Base.x = -References001.TurnCornLowDiam / 2
FEATURE [Part::MultiFuse] Fusion016  label="TC-Holes"
  Shapes = -> [Cylinder022,Cylinder021]
FEATURE [Part::Part2DObjectPython] Line006  label="GPU-GPU-Con"  # Draft 2D object (typed FeaturePython)
  ChamferSize = 0
  Closed = false
  End = (54,-251.25,94)
  FilletRadius = 0
  Length = 63.6946
  MakeFace = true
  Points = (2) [(78,-192.25,94),(54,-251.25,94)]
  Start = (78,-192.25,94)
  Subdivisions = 0
FEATURE [Part::Extrusion] Extrude015  label="GPU-GPU-Plane"
  Base = -> Line006
  Dir = (0,0,1)
  DirMode = 2
  FaceMakerClass = Part::FaceMakerBullseye
  LengthFwd = 60
  LengthRev = 0
  Solid = false
  Symmetric = false
FEATURE [Sketcher::SketchObject] Sketch001005018  label="GPU-GPU-Sketch"
  ExternalGeometry = -> [Extrude015]
  MapMode = 5
  Placement = pos=(134.026,-54.5191,0) rot=(0.724468,0.487415,0.487415;1.88767rad)
  Support = -> [Extrude015]
  expr: Constraints[13] = References.TurnCornXOffset + References.LargePlugOffset
  expr: Constraints[12] = References.TurnCornZOffset
  sketch-geometry (5):
    g0: LineSegment StartX=-199.885 StartY=115 StartZ=0 EndX=-161.19 EndY=115 EndZ=0
    g1: LineSegment StartX=-199.885 StartY=94 StartZ=0 EndX=-199.885 EndY=115 EndZ=0
    g2: LineSegment StartX=-212.385 StartY=94 StartZ=0 EndX=-199.885 EndY=94 EndZ=0
    g3: LineSegment StartX=-161.19 StartY=94 StartZ=0 EndX=-148.69 EndY=94 EndZ=0
    g4: LineSegment StartX=-161.19 StartY=115 StartZ=0 EndX=-161.19 EndY=94 EndZ=0
  constraints (14):
    c: Coincident(g4,g3)
    c: Coincident(g1,g2)
    c: Coincident(g1,g0)
    c: Coincident(g0,g4)
    c: Coincident(g3,g-3)
    c: Coincident(g-4,g2)
    c: Horizontal(g2)
    c: Vertical(g1)
    c: Vertical(g4)
    c: Horizontal(g3)
    c: Equal(g4,g1)
    c: Equal(g3,g2)
    c: Distance(g4) = 21
    c: Distance(g2) = 12.5
FEATURE [Part::Part2DObjectPython] Circle030  label="GPU-1-Adapter-Out"  # Draft 2D object (typed FeaturePython)
  FirstAngle = 0
  LastAngle = 0
  MakeFace = true
  Placement = pos=(58.75,-239.75,115) rot=(-0.962703,0.191314,-0.191314;1.6088rad)
  Radius = 8
  expr: Radius = References.LargeTubeOuterDiam / 2
FEATURE [Part::Part2DObjectPython] Circle031  label="GPU-2-Adapter-In"  # Draft 2D object (typed FeaturePython)
  FirstAngle = 0
  LastAngle = 0
  MakeFace = true
  Placement = pos=(74.18,-201.49,115) rot=(-0.962703,0.191314,-0.191314;1.6088rad)
  Radius = 8
  expr: Radius = References.LargeTubeOuterDiam / 2
FEATURE [TechDraw::DrawViewPart] View
  CoarseView = false
  Direction = (-22.75,-74.25,0)
  Focus = 100
  HardHidden = false
  IsoCount = 0
  IsoHidden = false
  IsoVisible = false
  LockPosition = false
  Perspective = false
  Rotation = 0
  ScaleType = 0
  SeamHidden = false
  SeamVisible = false
  SmoothHidden = false
  SmoothVisible = false
  Source = -> [Sweep016]
  X = 68.5204
  Y = 99.2261
FEATURE [TechDraw::DrawViewPart] View009
  CoarseView = false
  Direction = (-22.75,-74.25,0)
  Focus = 100
  HardHidden = false
  IsoCount = 0
  IsoHidden = false
  IsoVisible = false
  LockPosition = false
  Perspective = false
  Rotation = 0
  ScaleType = 0
  SeamHidden = false
  SeamVisible = false
  SmoothHidden = false
  SmoothVisible = false
  Source = -> [Sweep015]
  X = 167.96
  Y = 188.615
FEATURE [TechDraw::DrawViewAnnotation] Annotation008
  Font = osifont
  LineSpace = 80
  LockPosition = false
  MaxWidth = -1
  Rotation = 0
  ScaleType = 0
  Text = Side
  TextSize = 8
  TextStyle = 0
  X = 223.989
  Y = 117.403
FEATURE [TechDraw::DrawViewAnnotation] Annotation009
  Font = osifont
  LineSpace = 80
  LockPosition = false
  MaxWidth = -1
  Rotation = 0
  ScaleType = 0
  Text = Unbend
  TextSize = 8
  TextStyle = 0
  X = 224.844
  Y = 183.91
FEATURE [TechDraw::DrawViewPart] View010
  CoarseView = false
  Direction = (47.25,-47,0)
  Focus = 100
  HardHidden = false
  IsoCount = 0
  IsoHidden = false
  IsoVisible = false
  LockPosition = false
  Perspective = false
  Rotation = 0
  ScaleType = 0
  SeamHidden = false
  SeamVisible = false
  SmoothHidden = false
  SmoothVisible = false
  X = 128.398
  Y = 115.051
FEATURE [TechDraw::DrawViewPart] View011
  CoarseView = false
  Direction = (47.25,-47,0)
  Focus = 100
  HardHidden = false
  IsoCount = 0
  IsoHidden = false
  IsoVisible = false
  LockPosition = false
  Perspective = false
  Rotation = 0
  ScaleType = 0
  SeamHidden = false
  SeamVisible = false
  SmoothHidden = false
  SmoothVisible = false
  X = 125.404
  Y = 180.275
FEATURE [TechDraw::DrawViewDimension] Dimension070
  Arbitrary = false
  FormatSpec = %.2f
  LockPosition = false
  MeasureType = 1
  OverTolerance = 0
  References2D = -> [View010]
  Rotation = 0
  ScaleType = 0
  Type = 1
  UnderTolerance = 0
  X = 12.4033
  Y = 1.61303
FEATURE [TechDraw::DrawViewDimension] Dimension071
  Arbitrary = false
  FormatSpec = %.2f
  LockPosition = false
  MeasureType = 1
  OverTolerance = 0
  References2D = -> [View010]
  Rotation = 0
  ScaleType = 0
  Type = 2
  UnderTolerance = 0
  X = 11.7873
  Y = -20.6222
FEATURE [TechDraw::DrawViewDimension] Dimension074
  Arbitrary = false
  FormatSpec = %.2f
  LockPosition = false
  MeasureType = 1
  OverTolerance = 0
  References2D = -> [View011]
  Rotation = 0
  ScaleType = 0
  Type = 1
  UnderTolerance = 0
  X = -0.853411
  Y = -18.4758
FEATURE [TechDraw::DrawSVGTemplate] Template003
  EditableTexts = Designed_by_Name=Christoph <owner>; Drawing_number=1; FC-Date=Date; FC-SC=1:1; FC-SH=5; FC-Title=PC Water Cooling; Subtitle=GPU - GPU - Tube; Weight=Weight
  Height = 210
  Orientation = 1
  Width = 297
FEATURE [TechDraw::DrawSVGTemplate] Template004
  EditableTexts = Designed_by_Name=Christoph <owner>; Drawing_number=1; FC-Date=Date; FC-SC=1:1; FC-SH=4; FC-Title=PC Water Cooling; Subtitle=CPU - Chipset - Tube; Weight=Weight
  Height = 210
  Orientation = 1
  Width = 297
FEATURE [TechDraw::DrawSVGTemplate] Template005
  EditableTexts = Designed_by_Name=Christoph <owner>; Drawing_number=1; FC-Date=Date; FC-SC=1:1; FC-SH=1; FC-Title=PC Water Cooling; Subtitle=VRM - VRM - Tube; Weight=Weight
  Height = 210
  Orientation = 1
  Width = 297
FEATURE [TechDraw::DrawViewDimension] Dimension075
  Arbitrary = false
  FormatSpec = %.2f
  LockPosition = false
  MeasureType = 1
  OverTolerance = 0
  References2D = -> [View]
  Rotation = 0
  ScaleType = 0
  Type = 2
  UnderTolerance = 0
  X = -28.9793
  Y = 15.1598
FEATURE [TechDraw::DrawViewDimension] Dimension076
  Arbitrary = false
  FormatSpec = %.2f
  LockPosition = false
  MeasureType = 1
  OverTolerance = 0
  References2D = -> [View]
  Rotation = 0
  ScaleType = 0
  Type = 2
  UnderTolerance = 0
  X = 24.4884
  Y = -18.4792
FEATURE [TechDraw::DrawViewDimension] Dimension077
  Arbitrary = false
  FormatSpec = %.2f
  LockPosition = false
  MeasureType = 1
  OverTolerance = 0
  References2D = -> [View]
  Rotation = 0
  ScaleType = 0
  Type = 1
  UnderTolerance = 0
  X = 0.641548
  Y = 51.3192
FEATURE [TechDraw::DrawViewDimension] Dimension078
  Arbitrary = false
  FormatSpec = %.2f
  LockPosition = false
  MeasureType = 1
  OverTolerance = 0
  References2D = -> [View]
  Rotation = 0
  ScaleType = 0
  Type = 2
  UnderTolerance = 0
  X = 50.1939
  Y = 1.17582
FEATURE [TechDraw::DrawViewDimension] Dimension079
  Arbitrary = false
  FormatSpec = %.2f
  LockPosition = false
  MeasureType = 1
  OverTolerance = 0
  References2D = -> [View]
  Rotation = 0
  ScaleType = 0
  Type = 1
  UnderTolerance = 0
  X = 4.70468
  Y = -75.8723
FEATURE [TechDraw::DrawViewDimension] Dimension080
  Arbitrary = false
  FormatSpec = %.2f
  LockPosition = false
  MeasureType = 1
  OverTolerance = 0
  References2D = -> [View009]
  Rotation = 0
  ScaleType = 0
  Type = 1
  UnderTolerance = 0
  X = 1.06925
  Y = -11.3462
FEATURE [TechDraw::DrawViewDimension] Dimension081
  Arbitrary = false
  FormatSpec = %.2f
  LockPosition = false
  MeasureType = 1
  OverTolerance = 0
  References2D = -> [View]
  Rotation = 0
  ScaleType = 0
  Type = 2
  UnderTolerance = 0
  X = -52.3324
  Y = 53.9289
FEATURE [TechDraw::DrawViewDimension] Dimension082
  Arbitrary = false
  FormatSpec = %.2f
  LockPosition = false
  MeasureType = 1
  OverTolerance = 0
  References2D = -> [View]
  Rotation = 0
  ScaleType = 0
  Type = 1
  UnderTolerance = 0
  X = -28.1674
  Y = 75.1
FEATURE [Part::Sweep] Sweep017  label="GPU-GPU-Tube"
  Frenet = false
  Sections = -> [Circle030]
  Solid = false
  Spine = -> Sketch001005018 [Edge3]
  Transition = 1
FEATURE [TechDraw::DrawViewPart] View012
  CoarseView = false
  Direction = (-58,24,0)
  Focus = 100
  HardHidden = false
  IsoCount = 0
  IsoHidden = false
  IsoVisible = false
  LockPosition = false
  Perspective = false
  Rotation = 0
  ScaleType = 0
  SeamHidden = false
  SeamVisible = false
  SmoothHidden = false
  SmoothVisible = false
  Source = -> [Sweep017]
  X = 142.085
  Y = 135.153
FEATURE [TechDraw::DrawViewDimension] Dimension
  Arbitrary = false
  FormatSpec = %.2f
  LockPosition = false
  MeasureType = 1
  OverTolerance = 0
  References2D = -> [View012]
  Rotation = 0
  ScaleType = 0
  Type = 1
  UnderTolerance = 0
  X = 1.71079
  Y = -24.6802
FEATURE [Part::Cylinder] Cylinder023  label="ExtensionBase"
  Angle = 360
  AttacherType = Attacher::AttachEngine3D
  Height = 7
  Radius = 8.5
  expr: Height = References.ExtensionHeight
  expr: Radius = References.ExtensionDiamater / 2
FEATURE [Part::Cylinder] Cylinder024  label="LargePlugHole"
  Angle = 360
  AttacherType = Attacher::AttachEngine3D
  Height = 2.5
  Radius = 5
  expr: Radius = References.SmallTubeInnerDiam / 2
  expr: Height = References.LargePlugOffset
FEATURE [Part::Cylinder] Cylinder025  label="ExtensionHole"
  Angle = 360
  AttacherType = Attacher::AttachEngine3D
  Height = 7
  Radius = 5
  expr: Height = References.ExtensionHeight
  expr: Radius = References.SmallTubeInnerDiam / 2
FEATURE [Part::Cut] Cut006  label="Extension"
  Base = -> Cylinder023
  Tool = -> Cylinder025
FEATURE [Part::Cylinder] Cylinder026  label="LargePlugWallBase"
  Angle = 360
  AttacherType = Attacher::AttachEngine3D
  Height = 12.5
  Placement = pos=(0,0,2.5) rot=(0,0,1;0.017453rad)
  Radius = 12
  expr: Placement.Base.z = References.LargePlugOffset
  expr: Height = References.LargePlugHeight - References.LargePlugOffset
  expr: Radius = References.LargePlugDiam / 2
FEATURE [Part::Cylinder] Cylinder027  label="LargePlugWallHole"
  Angle = 360
  AttacherType = Attacher::AttachEngine3D
  Height = 12.5
  Placement = pos=(0,0,2.5) rot=(0,0,1;0rad)
  Radius = 8
  expr: Placement.Base.z = References.LargePlugOffset
  expr: Height = References.LargePlugHeight - References.LargePlugOffset
  expr: Radius = References.LargeTubeOuterDiam / 2
FEATURE [Part::Cut] Cut007  label="LargePlugWall"
  Base = -> Cylinder026
  Tool = -> Cylinder027
FEATURE [Part::Cut] Cut008  label="LargePlugBase001"
  Base = -> Cylinder019
  Tool = -> Cylinder024
FEATURE [Part::MultiFuse] Fusion017  label="LargePlug"
  Shapes = -> [Cut007,Cut008]
FEATURE [Part::Fillet] Fillet  label="TC-Top"
  Base = -> Box007
  Edges = 5 edges r=8.5: [Edge1,Edge2,Edge3,Edge10,Edge12]
FEATURE [Part::MultiFuse] Fusion018  label="TC-Body"
  Shapes = -> [Fillet,Cylinder020]
FEATURE [Part::Cut] Cut009  label="TurnableCorner"
  Base = -> Fusion018
  Tool = -> Fusion016
FEATURE [Sketcher::SketchObject] Sketch001005019  label="LargePlugSketch"
  MapMode = 5
  Placement = pos=(0,0,2.5) rot=(0,0,1;0rad)
  Support = -> [Fusion017]
  expr: Constraints[1] = References.LargeTubeOuterDiam
  sketch-geometry (1):
    g0: Circle CenterX=0 CenterY=0 CenterZ=0 NormalX=0 NormalY=0 NormalZ=1 AngleXU=0 Radius=8
  constraints (2):
    c: Coincident(g-1,g0)
    c: Diameter(g0) = 16
FEATURE [Part::Cylinder] Cylinder028  label="SmallPlugBase"
  Angle = 360
  AttacherType = Attacher::AttachEngine3D
  Height = 3
  Radius = 9.25
  expr: Height = References.SmallPlugOffset
  expr: Radius = References.SmallPlugDiam / 2
FEATURE [Part::Cylinder] Cylinder029  label="SmallPlugWallHole"
  Angle = 360
  AttacherType = Attacher::AttachEngine3D
  Height = 9
  Placement = pos=(0,0,2.5) rot=(0,0,1;0rad)
  Radius = 6
  expr: Placement.Base.z = References.LargePlugOffset
  expr: Height = References.SmallPlugHeight - References.SmallPlugOffset
  expr: Radius = References.SmallTubeOuterDiam / 2
FEATURE [Part::Cylinder] Cylinder030  label="SmallPlugWallBase"
  Angle = 360
  AttacherType = Attacher::AttachEngine3D
  Height = 9
  Placement = pos=(0,0,2.5) rot=(0,0,1;0.017453rad)
  Radius = 9.25
  expr: Placement.Base.z = References.LargePlugOffset
  expr: Height = References.SmallPlugHeight - References.SmallPlugOffset
  expr: Radius = References.SmallPlugDiam / 2
FEATURE [Part::Cut] Cut010  label="SmallPlugWall"
  Base = -> Cylinder030
  Tool = -> Cylinder029
FEATURE [Part::Cylinder] Cylinder031  label="SmallPlugHole"
  Angle = 360
  AttacherType = Attacher::AttachEngine3D
  Height = 3
  Radius = 5
  expr: Radius = References.SmallTubeInnerDiam / 2
  expr: Height = References.SmallPlugOffset
FEATURE [Part::Cut] Cut011  label="SmallPlugBas"
  Base = -> Cylinder028
  Tool = -> Cylinder031
FEATURE [Part::MultiFuse] Fusion019  label="SmallPlug"
  Shapes = -> [Cut010,Cut011]
FEATURE [Sketcher::SketchObject] Sketch001005020  label="SmallPlugSketch"
  MapMode = 5
  Placement = pos=(0,0,3) rot=(0,0,1;0rad)
  Support = -> [Fusion019]
  expr: Constraints[1] = References.SmallTubeOuterDiam
  sketch-geometry (1):
    g0: Circle CenterX=0 CenterY=0 CenterZ=0 NormalX=0 NormalY=0 NormalZ=1 AngleXU=0 Radius=6
  constraints (2):
    c: Coincident(g0,g-1)
    c: Diameter(g0) = 12
FEATURE [Part::MultiFuse] Fusion020  label="SmallPlug001"
  Placement = pos=(10,0,21) rot=(0,1,0;1.5708rad)
  Shapes = -> [Cut010,Cut011]
  expr: Placement.Base.x = References.TurnCornXOffset
  expr: Placement.Base.z = References.TurnCornZOffset
FEATURE [Part::Cut] Cut012  label="TurnableCorner001"
  Base = -> Fusion018
  Tool = -> Fusion016
FEATURE [Part::MultiFuse] Fusion021  label="CPU-In-Adapter"
  Placement = pos=(74,-75.75,-2.5) rot=(0,0,-1;1.5708rad)
  Refine = true
  Shapes = -> [Cut012,Fusion020]
  expr: Placement.Base.z = 0.5mm - References.SmallPlugOffset
FEATURE [Part::MultiFuse] Fusion022  label="Chipset-Out-Adapter"
  Placement = pos=(149.75,-215,-4.5) rot=(0,0,-1;0rad)
  Refine = true
  Shapes = -> [Cut012,Fusion020]
  expr: Placement.Base.z = -1.5mm - References.SmallPlugOffset
FEATURE [Part::MultiFuse] Fusion023  label="GPU2-Out-Adapter"
  Placement = pos=(54,-192.254,94) rot=(0,0,1;0rad)
  Refine = true
  Shapes = -> [Cut010,Cut011]
  expr: Placement.Base.z = 97mm - References.SmallPlugOffset
FEATURE [Part::MultiFuse] Fusion024  label="Chipset-In-Adapter"
  Placement = pos=(128.25,-215,-4.5) rot=(0,0,1;0rad)
  Refine = true
  Shapes = -> [Cut010,Cut011]
  expr: Placement.Base.z = -1.5mm - References.SmallPlugOffset
FEATURE [Part::MultiFuse] Fusion025  label="LargePlug003"
  Placement = pos=(10,0,21) rot=(0,1,0;1.5708rad)
  Shapes = -> [Cut007,Cut008]
  expr: Placement.Base.z = References.TurnCornZOffset
  expr: Placement.Base.x = References.TurnCornXOffset
FEATURE [Part::Cut] Cut013  label="TurnableCorner002"
  Base = -> Fusion018
  Tool = -> Fusion016
FEATURE [Part::MultiFuse] Fusion  label="GPU2-In-Adapter"
  Placement = pos=(78,-192.25,94) rot=(0,0,-1;1.96315rad)
  Refine = true
  Shapes = -> [Fusion025,Cut013]
  expr: Placement.Rotation.Angle = 67.52 - 180
FEATURE [Part::MultiFuse] Fusion026  label="GPU1-Out-Adapter"
  Placement = pos=(54,-251.25,94) rot=(0,0,1;1.17845rad)
  Refine = true
  Shapes = -> [Fusion025,Cut013]
FEATURE [Part::MultiFuse] Fusion027  label="VRM1-Out-Adapter"
  Placement = pos=(47,0,-2.5) rot=(0,0,1;0rad)
  Shapes = -> [Cut007,Cut008]
  expr: Placement.Base.z = -References.LargePlugOffset
FEATURE [Part::MultiFuse] Fusion028  label="VRM2-In-Adapter"
  Placement = pos=(0,-47.75,-2.5) rot=(0,0,1;0rad)
  Shapes = -> [Cut007,Cut008]
  expr: Placement.Base.z = -References.LargePlugOffset
FEATURE [Part::MultiFuse] Fusion029  label="VRM2-Out-Adapter"
  Placement = pos=(0,-82.75,-2.5) rot=(0,0,1;0rad)
  Shapes = -> [Cut007,Cut008]
  expr: Placement.Base.z = -References.LargePlugOffset
FEATURE [Part::MultiFuse] Fusion030  label="CPU-Out-Adapter"
  Placement = pos=(74,-54,-1.5) rot=(0,0,1;0rad)
  Shapes = -> [Cut010,Cut011]
  expr: Placement.Base.z = 1.5mm - References.SmallPlugOffset
FEATURE [Part::MultiFuse] Fusion031  label="VRM1-In-Adapter"
  Placement = pos=(82,0,-2.5) rot=(0,0,1;0rad)
  Shapes = -> [Cut010,Cut011]
  expr: Placement.Base.z = 0.5mm - References.SmallPlugOffset
FEATURE [Part::MultiFuse] Fusion032  label="GPU1-In-Adapter"
  Placement = pos=(78,-251.25,94) rot=(0,0,-1;1.96315rad)
  Refine = true
  Shapes = -> [Fusion025,Cut013]
  expr: Placement.Rotation.Angle = 180 - 67.52
FEATURE [TechDraw::DrawViewPart] View013
  CoarseView = false
  Direction = (0,0,1)
  Focus = 100
  HardHidden = false
  IsoCount = 0
  IsoHidden = false
  IsoVisible = false
  LockPosition = false
  Perspective = false
  Rotation = 0
  ScaleType = 0
  SeamHidden = false
  SeamVisible = false
  SmoothHidden = false
  SmoothVisible = false
  Source = -> [Sweep016]
  X = 192.839
  Y = 116.694
FEATURE [TechDraw::DrawViewAnnotation] Annotation
  Font = MS Shell Dlg 2
  LineSpace = 80
  LockPosition = false
  MaxWidth = -1
  Rotation = 0
  ScaleType = 0
  Text = Top
  TextSize = 8
  TextStyle = 0
  X = 196.493
  Y = 81.3689
FEATURE [TechDraw::DrawViewAnnotation] Annotation010
  Font = MS Shell Dlg 2
  LineSpace = 80
  LockPosition = false
  MaxWidth = -1
  Rotation = 0
  ScaleType = 0
  Text = Side
  TextSize = 8
  TextStyle = 0
  X = 59.0916
  Y = 88.4339
FEATURE [TechDraw::DrawViewAnnotation] Annotation011
  Font = MS Shell Dlg 2
  LineSpace = 80
  LockPosition = false
  MaxWidth = -1
  Rotation = 0
  ScaleType = 0
  Text = Unbend
  TextSize = 8
  TextStyle = 0
  X = 199.416
  Y = 165.174
FEATURE [TechDraw::DrawPage] Page005  label="CPU-Chipset-Drawing"
  KeepUpdated = true
  ProjectionType = 0
  Template = -> Template004
  Views = -> [View,View009,Dimension075,Dimension076,Dimension077,Dimension078,Dimension079,Dimension080,Dimension081,Dimension082,View013,Annotation,Annotation010,Annotation011]
FEATURE [TechDraw::DrawViewDimension] Dimension083
  Arbitrary = false
  FormatSpec = %.2f
  LockPosition = false
  MeasureType = 1
  OverTolerance = 0
  References2D = -> [View012]
  Rotation = 0
  ScaleType = 0
  Type = 2
  UnderTolerance = 0
  X = 29.4242
  Y = -0.487239
FEATURE [TechDraw::DrawPage] Page004  label="GPU-GPU-Drawing"
  KeepUpdated = true
  ProjectionType = 0
  Template = -> Template003
  Views = -> [View012,Dimension,Dimension083]
FEATURE [TechDraw::DrawViewDimension] Dimension084
  Arbitrary = false
  FormatSpec = %.2f
  LockPosition = false
  MeasureType = 1
  OverTolerance = 0
  References2D = -> [View010]
  Rotation = 0
  ScaleType = 0
  Type = 1
  UnderTolerance = 0
  X = -25.1732
  Y = 32.2771
FEATURE [TechDraw::DrawViewDimension] Dimension085
  Arbitrary = false
  FormatSpec = %.2f
  LockPosition = false
  MeasureType = 1
  OverTolerance = 0
  References2D = -> [View010]
  Rotation = 0
  ScaleType = 0
  Type = 2
  UnderTolerance = 0
  X = -51.9713
  Y = 10.1193
FEATURE [TechDraw::DrawViewDimension] Dimension086
  Arbitrary = false
  FormatSpec = %.2f
  LockPosition = false
  MeasureType = 1
  OverTolerance = 0
  References2D = -> [View010]
  Rotation = 0
  ScaleType = 0
  Type = 1
  UnderTolerance = 0
  X = 0.730858
  Y = -45.2096
FEATURE [TechDraw::DrawViewDimension] Dimension087
  Arbitrary = false
  FormatSpec = %.2f
  LockPosition = false
  MeasureType = 1
  OverTolerance = 0
  References2D = -> [View010]
  Rotation = 0
  ScaleType = 0
  Type = 2
  UnderTolerance = 0
  X = 48.317
  Y = 0.119286
FEATURE [TechDraw::DrawPage] Page  label="VRM-VRM-Tube-Drawing"
  KeepUpdated = true
  ProjectionType = 0
  Template = -> Template005
  Views = -> [Annotation008,Annotation009,View010,View011,Dimension070,Dimension071,Dimension074,Dimension084,Dimension085,Dimension086,Dimension087]
FEATURE [TechDraw::DrawViewDimension] Dimension088
  Arbitrary = false
  FormatSpec = %.2f
  LockPosition = false
  MeasureType = 1
  OverTolerance = 0
  References2D = -> [View003]
  Rotation = 0
  ScaleType = 0
  Type = 1
  UnderTolerance = 0
  X = 0.974478
  Y = -27.8807
FEATURE [TechDraw::DrawViewDimension] Dimension089
  Arbitrary = false
  FormatSpec = %.2f
  LockPosition = false
  MeasureType = 1
  OverTolerance = 0
  References2D = -> [View003]
  Rotation = 0
  ScaleType = 0
  Type = 2
  UnderTolerance = 0
  X = -47.3532
  Y = 0.821775
FEATURE [TechDraw::DrawViewDimension] Dimension090
  Arbitrary = false
  FormatSpec = %.2f
  LockPosition = false
  MeasureType = 1
  OverTolerance = 0
  References2D = -> [View003]
  Rotation = 0
  ScaleType = 0
  Type = 1
  UnderTolerance = 0
  X = -17.8753
  Y = 31.6773
FEATURE [TechDraw::DrawViewDimension] Dimension091
  Arbitrary = false
  FormatSpec = %.2f
  LockPosition = false
  MeasureType = 1
  OverTolerance = 0
  References2D = -> [View003]
  Rotation = 0
  ScaleType = 0
  Type = 2
  UnderTolerance = 0
  X = 36.1271
  Y = 8.28987
FEATURE [TechDraw::DrawViewDimension] Dimension092
  Arbitrary = false
  FormatSpec = %.2f
  LockPosition = false
  MeasureType = 1
  OverTolerance = 0
  References2D = -> [View003]
  Rotation = 0
  ScaleType = 0
  Type = 2
  UnderTolerance = 0
  X = -15.4478
  Y = -18.0083
FEATURE [TechDraw::DrawViewDimension] Dimension093
  Arbitrary = false
  FormatSpec = %.2f
  LockPosition = false
  MeasureType = 1
  OverTolerance = 0
  References2D = -> [View003]
  Rotation = 0
  ScaleType = 0
  Type = 2
  UnderTolerance = 0
  X = 13.9861
  Y = -16.0274
FEATURE [TechDraw::DrawPage] Page001  label="CPU-VRM-Tube-Drawing"
  KeepUpdated = true
  ProjectionType = 0
  Template = -> Template001
  Views = -> [View002,View003,Annotation002,Annotation003,Dimension035,Dimension088,Dimension089,Dimension090,Dimension091,Dimension092,Dimension093]
FEATURE [Part::Box] Box  label="VRM-Cooler-Base"
  AttacherType = Attacher::AttachEngine3D
  Height = 17
  Length = 60
  Placement = pos=(0,-8.5,-17) rot=(0,0,1;0rad)
  Width = 17
  expr: Placement.Base.z = -17mm
  expr: Placement.Base.y = -17 / 2
FEATURE [Part::Fillet] Fillet001  label="VRM-Cool-Temp"
  Base = -> Box
  Edges = 4 edges r=1: [Edge1,Edge3,Edge5,Edge7]
FEATURE [Part::Fillet] Fillet002  label="VRM-Cooler-Body"
  Base = -> Fillet001
  Edges = 8 edges r=0.5: [Edge1,Edge4,Edge7,Edge8,Edge11,Edge16,Edge17,Edge20]
  Placement = pos=(35,0,-2.5) rot=(0,0,1;0rad)
  expr: Placement.Base.z = -References.LargePlugOffset
  expr: Placement.Base.x = 47mm - References.LargePlugDiam / 2
FEATURE [Part::Box] Box008  label="Cube"
  AttacherType = Attacher::AttachEngine3D
  Height = 2
  Length = 89
  Placement = pos=(0,-6.5,-2) rot=(0,0,1;0rad)
  Width = 15
  expr: Placement.Base.y = -15mm / 2 + 1mm
FEATURE [Part::Fillet] Fillet003  label="VRM-Cooler-Contact"
  Base = -> Box008
  Edges = 12 edges r=0.25: [Edge1,Edge2,Edge3,Edge4,Edge5,Edge6,Edge7,Edge8,Edge9,Edge10,Edge11,Edge12]
  Placement = pos=(20,0,-19.5) rot=(0,0,1;0rad)
  expr: Placement.Base.z = -(References.LargePlugOffset + 17mm)
FEATURE [Part::Fillet] Fillet004  label="VRM-Cooler-Body001"
  Base = -> Fillet001
  Edges = 8 edges r=0.5: [Edge1,Edge4,Edge7,Edge8,Edge11,Edge16,Edge17,Edge20]
  Placement = pos=(0,-94.75,-2.5) rot=(0,0,1;1.5708rad)
  expr: Placement.Base.z = -References.LargePlugOffset
  expr: Placement.Base.y = -82.75mm - References.LargePlugDiam / 2
FEATURE [Part::Box] Box009  label="Cube001"
  AttacherType = Attacher::AttachEngine3D
  Height = 2
  Length = 94
  Placement = pos=(-94,-6.5,-2) rot=(0,0,1;0rad)
  Width = 15
  expr: Length = 60mm + 19mm + 15mm
  expr: Placement.Base.y = -15mm / 2 + 1mm
FEATURE [Part::Fillet] Fillet005  label="VRM-Cooler-Contact001"
  Base = -> Box009
  Edges = 12 edges r=0.25: [Edge1,Edge2,Edge3,Edge4,Edge5,Edge6,Edge7,Edge8,Edge9,Edge10,Edge11,Edge12]
  Placement = pos=(0,-16.75,-19.5) rot=(0,0,1;1.5708rad)
  expr: Placement.Base.y = -47.75mm + References.LargePlugDiam / 2 + 19mm
FEATURE [Part::MultiFuse] Fusion034  label="VRM-Cooler-2"
  Shapes = -> [Fillet004,Fillet005]
FEATURE [Part::MultiFuse] Fusion035  label="VRM-Cooler-1"
  Shapes = -> [Fillet003,Fillet002]
FEATURE [Part::Box] Box010  label="Mainboard"
  AttacherType = Attacher::AttachEngine3D
  Height = 2
  Length = 245
  Placement = pos=(-55,-296.5,-24.5) rot=(0,0,1;0rad)
  Width = 305
  expr: Placement.Base.z = -20mm - References.LargePlugOffset - 2mm
  expr: Placement.Base.x = 47mm - 90mm - References.LargePlugDiam / 2
  expr: Placement.Base.y = -305mm + 17mm / 2
FEATURE [Part::Box] Box011  label="MB-Connections"
  AttacherType = Attacher::AttachEngine3D
  Height = 56
  Length = 17
  Placement = pos=(-74,-142.25,-29.5) rot=(0,0,1;0rad)
  Width = 160.75
  expr: Placement.Base.z = -20mm - 7mm - References.LargePlugOffset
  expr: Placement.Base.y = -160.75mm + 17mm / 2 + 10mm
  expr: Placement.Base.x = -17mm - 43mm - References.LargePlugDiam / 2 - 2mm
FEATURE [Part::Box] Box012  label="Slots"
  AttacherType = Attacher::AttachEngine3D
  Height = 115
  Length = 17
  Placement = pos=(-74,-313.25,-29.5) rot=(0,0,1;0rad)
  Width = 171
  expr: Placement.Base.z = -20mm - 7mm - References.LargePlugOffset
  expr: Placement.Base.y = -160.75mm + 17mm / 2 + 10mm - 171mm
FEATURE [Part::Box] Box013  label="Back"
  AttacherType = Attacher::AttachEngine3D
  Height = 203
  Length = 1
  Placement = pos=(-74,-426,-45.5) rot=(0,0,1;0rad)
  Width = 457.5
  expr: Placement.Base.z = -20mm - 7mm - References.LargePlugOffset - 16mm
  expr: Placement.Base.x = -109mm + 47mm - References.LargePlugDiam / 2
  expr: Placement.Base.y = -457.5mm + 17mm / 2 + 13mm + 10mm
FEATURE [Part::Box] Box014  label="CPU-Cooler-Base"
  AttacherType = Attacher::AttachEngine3D
  Height = 14.5
  Length = 59
  Placement = pos=(44.5,-105.25,-18) rot=(0,0,1;0rad)
  Width = 60
  expr: Placement.Base.z = 6.5mm - 24.5mm
  expr: Placement.Base.x = 95.25mm - References.LargePlugDiam / 2 - References.SmallPlugDiam / 2 - 59mm / 2
  expr: Placement.Base.y = -36mm - 60mm - References.SmallPlugDiam / 2
FEATURE [Sketcher::SketchObject] Sketch001005021
  ExternalGeometry = -> [Box014]
  MapMode = 5
  Placement = pos=(44.5,-45.25,-18) rot=(0,0.707107,0.707107;3.14159rad)
  Support = -> [Box014]
  sketch-geometry (6):
    g0: LineSegment [constr] StartX=-59 StartY=14.5 StartZ=0 EndX=-45.25 EndY=14.5 EndZ=0
    g1: LineSegment [constr] StartX=0 StartY=14.5 StartZ=0 EndX=-13.75 EndY=14.5 EndZ=0
    g2: LineSegment StartX=-45.25 StartY=14.5 StartZ=0 EndX=-13.75 EndY=14.5 EndZ=0
    g3: LineSegment StartX=-43 StartY=16.5 StartZ=0 EndX=-16 EndY=16.5 EndZ=0
    g4: LineSegment StartX=-43 StartY=16.5 StartZ=0 EndX=-45.25 EndY=14.5 EndZ=0
    g5: LineSegment StartX=-16 StartY=16.5 StartZ=0 EndX=-13.75 EndY=14.5 EndZ=0
  constraints (16):
    c: Horizontal(g0)
    c: Horizontal(g1)
    c: Equal(g0,g1)
    c: Coincident(g1,g-4)
    c: Coincident(g0,g-3)
    c: Coincident(g0,g2)
    c: Coincident(g2,g1)
    c: Distance(g2) = 31.5
    c: Horizontal(g3)
    c: Coincident(g4,g3)
    c: Coincident(g5,g3)
    c: Coincident(g5,g2)
    c: Coincident(g4,g2)
    c: Equal(g5,g4)
    c: Distance(g3) = 27
    c: Distance(g3,g2) = 2
FEATURE [Part::Extrusion] Extrude016  label="CPU-Cooler-Top"
  Base = -> Sketch001005021
  Dir = (0,1,-2e-16)
  DirMode = 2
  FaceMakerClass = Part::FaceMakerBullseye
  LengthFwd = 60
  LengthRev = 0
  Reversed = true
  Solid = true
  Symmetric = false
FEATURE [Part::MultiFuse] Fusion036  label="CPU-Cooler"
  Shapes = -> [Box014,Extrude016]
FEATURE [Part::Box] Box015  label="Power-Supply"
  AttacherType = Attacher::AttachEngine3D
  Height = 148
  Length = 182
  Placement = pos=(-73,-409.5,-19.5) rot=(0,0,1;0rad)
  Width = 85
  expr: Placement.Base.x = -64.5mm - 17mm / 2
  expr: Placement.Base.y = -85mm - 12mm - 16mm - 305mm + 17mm / 2
  expr: Placement.Base.z = -20mm - 7mm + 10mm - References.LargePlugOffset
FEATURE [Part::Part2DObjectPython] Circle032  label="Flow-Sensor-Out"  # Draft 2D object (typed FeaturePython)
  FirstAngle = 0
  LastAngle = 0
  MakeFace = true
  Placement = pos=(-25,-303.75,119) rot=(0.57735,-0.57735,0.57735;4.18879rad)
  Radius = 8
  Support = -> [Box013]
  expr: Placement.Base.z = -29.5mm + 115mm + 42mm - 17mm / 2
  expr: Placement.Base.x = -74mm + 1mm - 12.5mm + 73mm - References.LargePlugHeight + References.LargePlugOffset
  expr: Placement.Base.y = -313.25mm + 17mm / 2 + 1mm
FEATURE [Sketcher::SketchObject] Sketch001005022  label="GPU-1-Adapter-In-Sketch"
  MapMode = 5
  Placement = pos=(73.2205,-262.8,94) rot=(0.962702,-0.191319,-0.191319;1.6088rad)
  Support = -> [Fusion032]
  expr: Constraints[2] = References.TurnCornZOffset
  expr: Constraints[0] = References.LargeTubeOuterDiam
  sketch-geometry (1):
    g0: Circle CenterX=0 CenterY=21 CenterZ=0 NormalX=0 NormalY=0 NormalZ=1 AngleXU=0 Radius=8
  constraints (3):
    c: Diameter(g0) = 16
    c: PointOnObject(g0,g-2)
    c: Distance(g-1,g0) = 21
FEATURE [Part::Part2DObjectPython] Circle033  label="GPU-1-Adapter-In"  # Draft 2D object (typed FeaturePython)
  FirstAngle = 0
  LastAngle = 0
  MakeFace = true
  Placement = pos=(73.2205,-262.8,115) rot=(0.962702,-0.191319,-0.191319;1.6088rad)
  Radius = 8
FEATURE [Part::Part2DObjectPython] Line007  label="Flow-Sensor-GPU-Con"  # Draft 2D object (typed FeaturePython)
  ChamferSize = 0
  Closed = false
  End = (73.22,-262.8,115)
  FilletRadius = 0
  Length = 106.49
  MakeFace = false
  Points = (2) [(-25,-303.75,119),(73.22,-262.8,115)]
  Start = (-25,-303.75,119)
  Subdivisions = 0
  expr: Start.x = -74mm + 1mm - 12.5mm + 73mm - References.LargePlugHeight + References.LargePlugOffset
FEATURE [Part::Extrusion] Extrude017  label="Flow-Sensor-GPU-1-Plane"
  Base = -> Line007
  Dir = (0,1,0)
  DirMode = 0
  FaceMakerClass = Part::FaceMakerBullseye
  LengthFwd = 30
  LengthRev = 0
  Reversed = true
  Solid = false
  Symmetric = false
FEATURE [Sketcher::SketchObject] Sketch001005023  label="Flow-Sensor-GPU-1-Sketch"
  ExternalGeometry = -> [Extrude017]
  MapMode = 5
  Placement = pos=(4.79684,0,117.787) rot=(0,1,0;0.040702rad)
  Support = -> [Extrude017]
  expr: Constraints[27] = References.LargeTubeBendDiam * (90 - 22.48) / 90 * pi / 4
  expr: Constraints[26] = References.UnbendOffset
  expr: Constraints[12] = References.LargeTubeBendDiam
  expr: Constraints[8] = 112.48 - 90
  expr: Constraints[2] = References.LargTubeStraightLen
  sketch-geometry (10):
    g0: LineSegment StartX=-29.8215 StartY=-303.75 StartZ=0 EndX=-9.82154 EndY=-303.75 EndZ=0
    g1: LineSegment StartX=68.4799 StartY=-262.8 StartZ=0 EndX=60.8327 EndY=-281.28 EndZ=0
    g2: LineSegment StartX=-9.82154 StartY=-303.75 StartZ=0 EndX=31.1474 EndY=-303.75 EndZ=0
    g3: ArcOfCircle CenterX=31.1474 CenterY=-273.25 CenterZ=0 NormalX=0 NormalY=0 NormalZ=1 AngleXU=0 Radius=30.5 StartAngle=4.71239 EndAngle=5.89084
    g4: LineSegment StartX=60.8327 StartY=-281.28 StartZ=0 EndX=59.3298 EndY=-284.912 EndZ=0
    g5: LineSegment StartX=-29.8215 StartY=-323.75 StartZ=0 EndX=-9.82154 EndY=-323.75 EndZ=0
    g6: LineSegment StartX=-9.82154 StartY=-323.75 StartZ=0 EndX=31.1474 EndY=-323.75 EndZ=0
    g7: LineSegment StartX=67.09 StartY=-323.75 StartZ=0 EndX=71.0204 EndY=-323.75 EndZ=0
    g8: LineSegment StartX=71.0204 StartY=-323.75 StartZ=0 EndX=91.0204 EndY=-323.75 EndZ=0
    g9: LineSegment StartX=31.1474 StartY=-323.75 StartZ=0 EndX=67.09 EndY=-323.75 EndZ=0
  constraints (29):
    c: Horizontal(g0)
    c: Coincident(g-3,g0)
    c: Distance(g0) = 20
    c: Equal(g1,g0)
    c: Coincident(g-4,g1)
    c: Horizontal(g2)
    c: Tangent(g3,g2) = -1.5708
    c: Coincident(g0,g2)
    c: Angle(g1,g-4) = 0.39235
    c: Coincident(g4,g1)
    c: Parallel(g4,g1)
    c: Tangent(g4,g3) = 1.5708
    c: Diameter(g3) = 61
    c: Horizontal(g6)
    c: Horizontal(g8)
    c: Horizontal(g9)
    c: Horizontal(g5)
    c: Horizontal(g7)
    c: Equal(g5,g0)
    c: Equal(g8,g1)
    c: Equal(g7,g4)
    c: Equal(g6,g2)
    c: Coincident(g6,g5)
    c: Coincident(g7,g8)
    c: Coincident(g6,g9)
    c: Coincident(g9,g7)
    c: Distance(g0,g5) = 20
    c: Distance(g9) = 35.9426
    c: PointOnObject(g5,g-3)
FEATURE [Part::Part2DObjectPython] Circle034  label="Flow-Sensor-GPU-1-Unbend-Start"  # Draft 2D object (typed FeaturePython)
  FirstAngle = 0
  LastAngle = 0
  MakeFace = true
  Placement = pos=(-14,-323.75,119) rot=(0.57735,-0.57735,0.57735;4.18879rad)
  Radius = 8
  Support = -> [Box013]
  expr: Placement.Base.z = -29.5mm + 115mm + 42mm - 17mm / 2
  expr: Placement.Base.x = -73mm + 71.5mm - References.LargePlugHeight + References.LargePlugOffset
  expr: Placement.Base.y = -313.25mm + 17mm / 2 + 1mm
FEATURE [Part::Sweep] Sweep018  label="Flow-Sensor-GPU-Unbend"
  Frenet = false
  Sections = -> [Circle034]
  Solid = false
  Spine = -> Sketch001005023 [Edge6,Edge7,Edge8,Edge9,Edge10]
  Transition = 1
FEATURE [Part::Sweep] Sweep019  label="Flow-Sensor-GPU-Tube"
  Frenet = false
  Sections = -> [Circle032]
  Solid = false
  Spine = -> Sketch001005023 [Edge1,Edge2,Edge3,Edge4,Edge5]
  Transition = 1
FEATURE [Part::MultiFuse] Fusion037  label="Tower-Back"
  Shapes = -> [Box011,Box012,Box013]
FEATURE [Part::MultiFuse] Fusion038  label="Flow-Sensor-Out-Adapter"
  Placement = pos=(-27.5,-303.75,119) rot=(0,1,0;1.5708rad)
  Shapes = -> [Cut007,Cut008]
  expr: Placement.Base.x = -74mm + 1mm - 12.5mm + 73mm - References.LargePlugHeight
FEATURE [Part::Cylinder] Cylinder  label="Flow-Sensor"
  Angle = 360
  AttacherType = Attacher::AttachEngine3D
  Height = 58
  Placement = pos=(-85.5,-303.75,119) rot=(0,1,0;1.5708rad)
  Radius = 8.5
  expr: Height = 73mm - References.LargePlugHeight
  expr: Placement.Base.x = -74mm + 1mm - 12.5mm
FEATURE [TechDraw::DrawSVGTemplate] Template006
  EditableTexts = Designed_by_Name=Christoph <owner>; Drawing_number=1; FC-Date=Date; FC-SC=1:1; FC-SH=6; FC-Title=PC Water Cooling; Subtitle=Flow-Sensor - GPU-1 - Tube; Weight=Weight
  Height = 210
  Orientation = 1
  Width = 297
FEATURE [TechDraw::DrawViewPart] View014
  CoarseView = false
  Direction = (0,0,1)
  Focus = 100
  HardHidden = false
  IsoCount = 0
  IsoHidden = false
  IsoVisible = false
  LockPosition = false
  Perspective = false
  Rotation = 0
  ScaleType = 0
  SeamHidden = false
  SeamVisible = false
  SmoothHidden = false
  SmoothVisible = false
  Source = -> [Sweep019]
  X = 173.394
  Y = 119.97
FEATURE [TechDraw::DrawViewPart] View015
  CoarseView = false
  Direction = (0,1,0)
  Focus = 100
  HardHidden = false
  IsoCount = 0
  IsoHidden = false
  IsoVisible = false
  LockPosition = false
  Perspective = false
  Rotation = 0
  ScaleType = 0
  SeamHidden = false
  SeamVisible = false
  SmoothHidden = false
  SmoothVisible = false
  Source = -> [Sweep019]
  X = 69.2929
  Y = 43.5812
FEATURE [TechDraw::DrawViewAnnotation] Annotation012
  Font = MS Shell Dlg 2
  LineSpace = 80
  LockPosition = false
  MaxWidth = -1
  Rotation = 0
  ScaleType = 0
  Text = Top
  TextSize = 8
  TextStyle = 0
  X = 180.124
  Y = 75.3529
FEATURE [TechDraw::DrawViewDimension] Dimension094
  Arbitrary = false
  FormatSpec = %.2f
  LockPosition = false
  MeasureType = 1
  OverTolerance = 0
  References2D = -> [View014]
  Rotation = 0
  ScaleType = 0
  Type = 1
  UnderTolerance = 0
  X = -23.2785
  Y = 1.26855
FEATURE [TechDraw::DrawViewDimension] Dimension095
  Arbitrary = false
  FormatSpec = %.2f
  LockPosition = false
  MeasureType = 1
  OverTolerance = 0
  References2D = -> [View014]
  Rotation = 0
  ScaleType = 0
  Type = 0
  UnderTolerance = 0
  X = 18.751
  Y = 21.5344
FEATURE [TechDraw::DrawViewDimension] Dimension096
  Arbitrary = false
  FormatSpec = %.2f
  LockPosition = false
  MeasureType = 1
  OverTolerance = 0
  References2D = -> [View014]
  Rotation = 0
  ScaleType = 0
  Type = 6
  UnderTolerance = 0
  X = 8.64706
  Y = 1.44118
FEATURE [TechDraw::DrawViewDimension] Dimension097
  Arbitrary = false
  FormatSpec = %.2f
  LockPosition = false
  MeasureType = 1
  OverTolerance = 0
  References2D = -> [View015]
  Rotation = 0
  ScaleType = 0
  Type = 2
  UnderTolerance = 0
  X = 49.717
  Y = -18.9118
FEATURE [TechDraw::DrawViewDimension] Dimension098
  Arbitrary = false
  FormatSpec = %.2f
  LockPosition = false
  MeasureType = 1
  OverTolerance = 0
  References2D = -> [View015]
  Rotation = 0
  ScaleType = 0
  Type = 2
  UnderTolerance = 0
  X = 50.3904
  Y = 20.3183
FEATURE [TechDraw::DrawViewPart] View016
  CoarseView = false
  Direction = (0,0,1)
  Focus = 100
  HardHidden = false
  IsoCount = 0
  IsoHidden = false
  IsoVisible = false
  LockPosition = false
  Perspective = false
  Rotation = 0
  ScaleType = 0
  SeamHidden = false
  SeamVisible = false
  SmoothHidden = false
  SmoothVisible = false
  Source = -> [Sweep018]
  X = 131.206
  Y = 181.588
FEATURE [TechDraw::DrawViewDimension] Dimension099
  Arbitrary = false
  FormatSpec = %.2f
  LockPosition = false
  MeasureType = 1
  OverTolerance = 0
  References2D = -> [View016]
  Rotation = 0
  ScaleType = 0
  Type = 1
  UnderTolerance = 0
  X = -0.247059
  Y = -21.0941
FEATURE [TechDraw::DrawViewAnnotation] Annotation013
  Font = MS Shell Dlg 2
  LineSpace = 80
  LockPosition = false
  MaxWidth = -1
  Rotation = 0
  ScaleType = 0
  Text = Unbend
  TextSize = 8
  TextStyle = 0
  X = 42.0176
  Y = 182.329
FEATURE [TechDraw::DrawViewAnnotation] Annotation014
  Font = MS Shell Dlg 2
  LineSpace = 80
  LockPosition = false
  MaxWidth = -1
  Rotation = 0
  ScaleType = 0
  Text = Side
  TextSize = 8
  TextStyle = 0
  X = 70.2318
  Y = 72.3882
FEATURE [TechDraw::DrawPage] Page006  label="Flow-Sensor-GPU-1-Drawing"
  KeepUpdated = true
  ProjectionType = 0
  Template = -> Template006
  Views = -> [View014,View015,Annotation012,Dimension094,Dimension095,Dimension096,Dimension097,Dimension098,View016,Dimension099,Annotation013,Annotation014]
FEATURE [App::DocumentObjectGroup] Group  label="Drawings"
  Group = -> [Page002,Page001,Page,Page004,Page005,Page006]
FEATURE [Part::Cylinder] Cylinder032  label="AGB"
  Angle = 360
  AttacherType = Attacher::AttachEngine3D
  Height = 190
  Placement = pos=(-120.5,-132.25,119) rot=(1,0,0;1.5708rad)
  Radius = 37
  expr: Radius = 37
  expr: Placement.Base.y = -303.75mm - 27mm + 17mm / 2 + 190mm
  expr: Placement.Base.x = -74mm + 1mm - 12.5mm + 2mm - 37mm
FEATURE [Part::Cylinder] Cylinder034  label="C-Bottom-Hole"
  Angle = 360
  AttacherType = Attacher::AttachEngine3D
  Height = 16
  Radius = 5
  expr: Radius = References.SmallTubeInnerDiam / 2
FEATURE [Part::Box] Box017  label="C-Top-Base"
  AttacherType = Attacher::AttachEngine3D
  Height = 19.5
  Length = 19
  Placement = pos=(-9,-9.5,0) rot=(0,0,1;0rad)
  Width = 18
  expr: Placement.Base.y = -References.CornLen / 2
  expr: Placement.Base.x = -References.CornWid / 2
FEATURE [Part::Fillet] Fillet006  label="C-Top"
  Base = -> Box017
  Edges = 5 edges r=8.5: [Edge1,Edge2,Edge3,Edge10,Edge12]
FEATURE [Part::Cylinder] Cylinder035  label="C-Top-Hole001"
  Angle = 360
  AttacherType = Attacher::AttachEngine3D
  Height = 15
  Placement = pos=(-5,0,11.5) rot=(0,1,0;1.5708rad)
  Radius = 5
  expr: Placement.Base.x = References.CornXOffset - 15mm
  expr: Placement.Base.z = References.CornZOffset
  expr: Radius = References.SmallTubeInnerDiam / 2
FEATURE [Part::MultiFuse] Fusion039  label="C-Holes"
  Shapes = -> [Cylinder034,Cylinder035]
FEATURE [Part::Cut] Cut  label="Corner"
  Base = -> Fillet006
  Tool = -> Fusion039
FEATURE [App::DocumentObjectGroup] Group007  label="Templates"
  Group = -> [Fusion017,Cut006,Sketch001005019,Fusion019,Cut009,Sketch001005020,Cut]
FEATURE [Part::Cut] Cut014  label="AGB-In-Corner"
  Base = -> Fillet006
  Placement = pos=(0,0,7) rot=(0,0,1;0rad)
  Tool = -> Fusion039
  expr: Placement.Base.z = References.ExtensionHeight
FEATURE [Part::MultiFuse] Fusion040  label="AGB-In-Plug"
  Placement = pos=(10,0,18.5) rot=(0,1,0;1.5708rad)
  Shapes = -> [Cut007,Cut008]
  expr: Placement.Base.x = References.CornXOffset
  expr: Placement.Base.z = References.CornZOffset + References.ExtensionHeight
FEATURE [Part::Cut] Cut015  label="AGB-In-Extension"
  Base = -> Cylinder023
  Tool = -> Cylinder025
FEATURE [Part::MultiFuse] Fusion041  label="AGB-In-Adapter"
  Placement = pos=(-95.7513,-303.75,94.2513) rot=(0.67956,0.678159,0.279819;2.59356rad)
  Refine = true
  Shapes = -> [Cut014,Fusion040,Cut015]
  expr: Placement.Base.z = 119mm - 35mm / sqrt(2)
  expr: Placement.Base.y = -303.75mm
  expr: Placement.Base.x = -74mm + 1mm - 12.5mm + 35mm * (-1 + 1 / sqrt(2))
FEATURE [Part::Box] Box018  label="Radiator"
  AttacherType = Attacher::AttachEngine3D
  Height = 86
  Length = 280
  Placement = pos=(-54,-141.5,63.5) rot=(0,0,1;0rad)
  Width = 124
  expr: Placement.Base.y = -124mm + 17mm / 2 + 13mm + 10mm - 49mm
  expr: Placement.Base.x = -74mm + 20mm
  expr: Placement.Base.z = -20mm - References.LargePlugOffset + 86mm
FEATURE [Sketcher::SketchObject] Sketch001005024  label="Radi-Out-Sketch"
  ExternalGeometry = -> [Box018]
  MapMode = 5
  Placement = pos=(-54,-141.5,63.5) rot=(0.57735,-0.57735,-0.57735;2.0944rad)
  Support = -> [Box018]
  expr: Constraints[6] = 39.5mm - References.TurnCornLowDiam / 2
  expr: Constraints[2] = 100mm - References.TurnCornLowDiam / 2
  expr: Constraints[5] = References.LargeTubeOuterDiam
  expr: Constraints[3] = 40mm - References.LargePlugDiam / 2
  sketch-geometry (4):
    g0: LineSegment [constr] StartX=-91 StartY=0 StartZ=0 EndX=-91 EndY=28 EndZ=0
    g1: Circle CenterX=-91 CenterY=28 CenterZ=0 NormalX=0 NormalY=0 NormalZ=1 AngleXU=0 Radius=8
    g2: LineSegment [constr] StartX=-30.5 StartY=0 StartZ=0 EndX=-30.5 EndY=28 EndZ=0
    g3: Circle CenterX=-30.5 CenterY=28 CenterZ=0 NormalX=0 NormalY=0 NormalZ=1 AngleXU=0 Radius=8
  constraints (12):
    c: Vertical(g0)
    c: PointOnObject(g0,g-1)
    c: Distance(g-1,g0) = 91
    c: Distance(g0) = 28
    c: Coincident(g1,g0)
    c: Diameter(g1) = 16
    c: Distance(g-1,g2) = 30.5
    c: PointOnObject(g2,g-1)
    c: Vertical(g2)
    c: Equal(g2,g0)
    c: Coincident(g3,g2)
    c: Equal(g3,g1)
FEATURE [Sketcher::SketchObject] Sketch001005025  label="Radi-in-Sketch"
  MapMode = 5
  Placement = pos=(-54,-141.5,63.5) rot=(1,0,0;3.14159rad)
  Support = -> [Box018]
  expr: Constraints[9] = 101.5mm - References.TurnCornLowDiam / 2
  expr: Constraints[3] = 40.5mm - References.TurnCornLowDiam / 2
  expr: Constraints[5] = References.LargeTubeOuterDiam
  expr: Constraints[2] = 2.5mm + References.LargePlugDiam / 2
  sketch-geometry (4):
    g0: LineSegment [constr] StartX=0 StartY=-31.5 StartZ=0 EndX=14.5 EndY=-31.5 EndZ=0
    g1: Circle CenterX=14.5 CenterY=-31.5 CenterZ=0 NormalX=0 NormalY=0 NormalZ=1 AngleXU=0 Radius=8
    g2: LineSegment [constr] StartX=0 StartY=-92.5 StartZ=0 EndX=14.5 EndY=-92.5 EndZ=0
    g3: Circle CenterX=14.5 CenterY=-92.5 CenterZ=0 NormalX=0 NormalY=0 NormalZ=1 AngleXU=0 Radius=8
  constraints (12):
    c: Horizontal(g0)
    c: PointOnObject(g0,g-2)
    c: Distance(g0) = 14.5
    c: Distance(g-1,g0) = 31.5
    c: Coincident(g1,g0)
    c: Diameter(g1) = 16
    c: Horizontal(g2)
    c: Equal(g2,g0)
    c: PointOnObject(g2,g-2)
    c: Distance(g-1,g2) = 92.5
    c: Coincident(g3,g2)
    c: Equal(g3,g1)
FEATURE [Part::Part2DObjectPython] Circle035  label="Radi-In"  # Draft 2D object (typed FeaturePython)
  FirstAngle = 0
  LastAngle = 0
  MakeFace = true
  Placement = pos=(-39.5,-110,63.5) rot=(1,0,0;3.14159rad)
  Radius = 8
FEATURE [Part::Part2DObjectPython] Circle038  label="Radi-Out"  # Draft 2D object (typed FeaturePython)
  FirstAngle = 0
  LastAngle = 0
  MakeFace = true
  Placement = pos=(-54,-50.5,91.5) rot=(0.57735,-0.57735,-0.57735;2.0944rad)
  Radius = 8
FEATURE [App::DocumentObjectGroup] Group001  label="Generated"
  Group = -> [Circle011,Circle010,Circle,Circle002,Circle003,Circle001,Line001,Circle015,Circle022,Circle023,Line005,Circle025,Circle026,Circle027,Circle028,Line006,Circle033,Line007,Circle032,Circle035,Circle038]
FEATURE [Part::Part2DObjectPython] Line008  label="VRM2-Radi-Con"  # Draft 2D object (typed FeaturePython)
  ChamferSize = 0
  Closed = false
  End = (-39.5,-110,63.5)
  FilletRadius = 0
  Length = 97.3014
  MakeFace = false
  Placement = pos=(-93.4472,61.7481,-14.5) rot=(-0.72696,0.485556,-0.485556;1.88441rad)
  Points = (2) [(136.939,-14.5,44.383),(179.314,-78,-15.9471)]
  Start = (0,-47.75,7.64e-14)
  Subdivisions = 0
FEATURE [Part::Extrusion] Extrude018  label="VRM2-Radi-Plane"
  Base = -> Line008
  Dir = (0,0,1)
  DirMode = 0
  FaceMakerClass = Part::FaceMakerBullseye
  LengthFwd = 30
  LengthRev = 0
  Solid = false
  Symmetric = false
FEATURE [Part::MultiFuse] Fusion042  label="Radi-In-Adapter"
  Placement = pos=(-39.5,-110,63.5) rot=(-0.872411,-0.488774,0;3.14159rad)
  Refine = true
  Shapes = -> [Fusion025,Cut013]
  expr: Placement.Rotation.Angle = 180 - 67.52
FEATURE [Sketcher::SketchObject] Sketch001005026  label="VRM-Radi-Sketch"
  ExternalGeometry = -> [Extrude018]
  MapMode = 5
  Placement = pos=(21.6016,-13.707,0) rot=(0.789449,0.434033,0.434033;1.80504rad)
  Support = -> [Extrude018]
  expr: Constraints[24] = References.UnbendOffset
  expr: Constraints[20] = References.LargeTubeBendDiam * pi / 4
  expr: Constraints[12] = References.LargeTubeBendDiam
  expr: Constraints[11] = References.TurnCornXOffset + References.LargePlugOffset
  expr: Constraints[10] = References.TurnCornZOffset
  sketch-geometry (9):
    g0: LineSegment [constr] StartX=-114.043 StartY=63.5 StartZ=0 EndX=-114.043 EndY=42.5 EndZ=0
    g1: LineSegment [constr] StartX=-114.043 StartY=42.5 StartZ=0 EndX=-101.543 EndY=42.5 EndZ=0
    g2: LineSegment StartX=-101.543 StartY=42.5 StartZ=0 EndX=-70.8181 EndY=42.5 EndZ=0
    g3: LineSegment StartX=-40.3181 StartY=6.13e-14 StartZ=0 EndX=-40.3181 EndY=12 EndZ=0
    g4: ArcOfCircle CenterX=-70.8181 CenterY=12 CenterZ=0 NormalX=0 NormalY=0 NormalZ=1 AngleXU=0 Radius=30.5 StartAngle=1.2e-15 EndAngle=1.5708
    g5: LineSegment StartX=-101.543 StartY=62.5 StartZ=0 EndX=-70.8181 EndY=62.5 EndZ=0
    g6: LineSegment StartX=-70.8181 StartY=62.5 StartZ=0 EndX=-22.9089 EndY=62.5 EndZ=0
    g7: LineSegment StartX=-22.9089 StartY=62.5 StartZ=0 EndX=-10.9089 EndY=62.5 EndZ=0
    g8: LineSegment [constr] StartX=-70.8181 StartY=62.5 StartZ=0 EndX=-70.8181 EndY=42.5 EndZ=0
  constraints (25):
    c: Vertical(g0)
    c: Horizontal(g1)
    c: Horizontal(g2)
    c: Coincident(g0,g1)
    c: Coincident(g1,g2)
    c: Coincident(g-3,g0)
    c: Tangent(g4,g2) = 1.5708
    c: Tangent(g4,g3) = -1.5708
    c: Vertical(g3)
    c: Coincident(g3,g-3)
    c: Distance(g0) = 21
    c: Distance(g1) = 12.5
    c: Diameter(g4) = 61
    c: Horizontal(g5)
    c: Horizontal(g6)
    c: Horizontal(g7)
    c: Coincident(g5,g6)
    c: Coincident(g6,g7)
    c: Equal(g5,g2)
    c: Equal(g7,g3)
    c: Distance(g6) = 47.9093
    c: Vertical(g8)
    c: Coincident(g8,g2)
    c: Coincident(g8,g5)
    c: Distance(g8) = 20
FEATURE [Part::Sweep] Sweep020  label="VRM2-Radi-Tube"
  Frenet = false
  Sections = -> [Circle001]
  Solid = false
  Spine = -> Sketch001005026 [Edge3,Edge2,Edge1]
  Transition = 1
FEATURE [Part::Part2DObjectPython] Line009  label="VRM-VRM-Con001"  # Draft 2D object (typed FeaturePython)
  ChamferSize = 0
  Closed = false
  End = (0,-82.7493,0)
  FilletRadius = 0
  Length = 95.1654
  MakeFace = true
  Points = (2) [(47,0,0),(0,-82.7493,0)]
  Start = (47,0,0)
  Subdivisions = 0
FEATURE [Part::Extrusion] Extrude  label="VRM-VRM-Plane"
  Base = -> Line009
  Dir = (0,0,1)
  DirMode = 2
  FaceMakerClass = Part::FaceMakerBullseye
  LengthFwd = 60
  LengthRev = 0
  Solid = false
  Symmetric = false
FEATURE [Sketcher::SketchObject] Sketch001005027  label="VRM-VRM-Sketch"
  ExternalGeometry = -> [Extrude]
  MapMode = 5
  Placement = pos=(35.536,-20.1838,0) rot=(0.772069,0.449394,0.449394;1.82664rad)
  Support = -> [Extrude]
  expr: Constraints[11] = References.LargTubeStraightLen
  expr: Constraints[4] = References.LargeTubeBendDiam
  sketch-geometry (5):
    g0: LineSegment StartX=23.2122 StartY=3.9e-15 StartZ=0 EndX=23.2122 EndY=20 EndZ=0
    g1: LineSegment StartX=-71.9532 StartY=-1.22e-14 StartZ=0 EndX=-71.9532 EndY=20 EndZ=0
    g2: LineSegment StartX=-41.4532 StartY=50.5 StartZ=0 EndX=-7.28778 EndY=50.5 EndZ=0
    g3: ArcOfCircle CenterX=-7.28778 CenterY=20 CenterZ=0 NormalX=0 NormalY=0 NormalZ=1 AngleXU=0 Radius=30.5 StartAngle=0 EndAngle=1.5708
    g4: ArcOfCircle CenterX=-41.4532 CenterY=20 CenterZ=0 NormalX=0 NormalY=0 NormalZ=1 AngleXU=0 Radius=30.5 StartAngle=1.5708 EndAngle=3.14159
  constraints (12):
    c: Vertical(g0)
    c: Vertical(g1)
    c: Horizontal(g2)
    c: Equal(g4,g3)
    c: Diameter(g3) = 61
    c: Tangent(g2,g3) = 1.5708
    c: Tangent(g2,g4) = 1.5708
    c: Tangent(g4,g1) = 1.5708
    c: Tangent(g3,g0) = -1.5708
    c: Coincident(g0,g-3)
    c: Coincident(g1,g-3)
    c: Distance(g0) = 20
FEATURE [Part::Sweep] Sweep021  label="VRM-VRM-Tube"
  Frenet = false
  Sections = -> [Circle002]
  Solid = false
  Spine = -> Sketch001005027 [Edge1,Edge2,Edge3,Edge4,Edge5]
  Transition = 1
FEATURE [Part::MultiFuse] Fusion043  label="Radi-Out-Adapter"
  Placement = pos=(-54,-50.5,91.5) rot=(0,1,0;-1.5708rad)
  Shapes = -> [Cut007,Cut008]
FEATURE [App::DocumentObjectGroup] Group005  label="OpticalSugar"
  Group = -> [Cut002,Fusion021,Fusion022,Fusion023,Fusion024,Fusion,Fusion026,Fusion027,Fusion028,Fusion029,Fusion030,Fusion031,Fusion032,Fusion034,Fusion035,Box010,Fusion036,Box015,Fusion037,Fusion038,Cylinder,Cylinder032,Fusion041,Box018,Fusion042,Fusion043]
FEATURE [Part::Part2DObjectPython] Circle042  label="Radi-Adapter-Out"  # Draft 2D object (typed FeaturePython)
  FirstAngle = 0
  LastAngle = 0
  MakeFace = true
  Placement = pos=(-56.5,-50.5,91.5) rot=(0.57735,-0.57735,-0.57735;2.0944rad)
  Radius = 8
  expr: Placement.Base.x = -54mm - References.LargePlugOffset
FEATURE [Part::Part2DObjectPython] Line011  label="Radi-AGB-Con-1"  # Draft 2D object (typed FeaturePython)
  ChamferSize = 0
  Closed = false
  End = (-82.6698,-303.75,81.1698)
  FilletRadius = 0
  Length = 253.832
  MakeFace = false
  Placement = pos=(-69,-50.4972,92.8564) rot=(0.57735,-0.57735,-0.57735;2.0944rad)
  Points = (2) [(3.80249e-06,-1.35642,0),(253.253,-11.6866,13.6698)]
  Start = (-69,-50.4972,91.5)
  Subdivisions = 0
  expr: End.z = 119mm - (35mm + References.ExtensionHeight + References.CornZOffset) / sqrt(2)
  expr: End.x = -74mm + 1mm - 12.5mm - 35mm + (35mm + References.ExtensionHeight + References.CornZOffset) / sqrt(2)
FEATURE [Part::Extrusion] Extrude020  label="Radi-AGB-Plane"
  Base = -> Line011
  Dir = (-1,0,0)
  DirMode = 2
  FaceMakerClass = Part::FaceMakerBullseye
  LengthFwd = 10
  LengthRev = 0
  Solid = false
  Symmetric = false
FEATURE [Sketcher::SketchObject] Sketch001005028  label="Radi-AGB-Sketch"
  ExternalGeometry = -> [Extrude020]
  MapMode = 5
  Placement = pos=(0,-3.80998,93.4044) rot=(1,0,0;0.040768rad)
  Support = -> [Extrude020]
  expr: Constraints[9] = References.LargeTubeBendDiam
  sketch-geometry (4):
    g0: LineSegment [constr] StartX=-69 StartY=-46.726 StartZ=0 EndX=-79 EndY=-46.726 EndZ=0
    g1: ArcOfCircle CenterX=-69 CenterY=-77.226 CenterZ=0 NormalX=0 NormalY=0 NormalZ=1 AngleXU=0 Radius=30.5 StartAngle=1.5708 EndAngle=3.90267
    g2: ArcOfCircle CenterX=-113.17 CenterY=-119.298 CenterZ=0 NormalX=0 NormalY=0 NormalZ=1 AngleXU=0 Radius=30.5 StartAngle=2e-16 EndAngle=0.761075
    g3: LineSegment StartX=-82.6698 StartY=-300.189 StartZ=0 EndX=-82.6698 EndY=-119.298 EndZ=0
  constraints (10):
    c: Tangent(g0,g1) = -1.5708
    c: Horizontal(g0)
    c: Coincident(g0,g-3)
    c: Distance(g0) = 10
    c: Vertical(g3)
    c: Coincident(g3,g-3)
    c: Tangent(g3,g2) = -1.5708
    c: Tangent(g2,g1) = 1.5708
    c: Equal(g2,g1)
    c: Diameter(g1) = 61
FEATURE [App::DocumentObjectGroup] Group002  label="Sketches"
  Group = -> [Sketch,Sketch001005005,Sketch001005004,Sketch001004,Sketch001005010,Sketch001005012,Sketch001005011,Sketch001005014,Sketch001005015,Sketch001005016,Sketch001005017,Sketch001005018,Sketch001005023,Sketch001005022,Sketch001005024,Sketch001005025,Sketch001005027,Sketch001005026,Sketch001005028]
FEATURE [Part::Part2DObjectPython] Circle043  label="AGB-In"  # Draft 2D object (typed FeaturePython)
  FirstAngle = 0
  LastAngle = 0
  MakeFace = true
  Placement = pos=(-95.2513,-303.75,94.2513) rot=(0.678915,0.678915,0.279553;2.59356rad)
  Radius = 8
  Support = -> [Fusion041]
  expr: Placement.Base.z = 119mm - 35mm / sqrt(2)
  expr: Placement.Base.x = -73mm - 2mm - 9mm - 1mm + 35mm * (-1 + 1 / sqrt(2))
  expr: Placement.Base.y = -303.75mm
  expr: Radius = References.LargeTubeOuterDiam / 2
FEATURE [Part::Part2DObjectPython] Line012  label="Radi-AGB-Con"  # Draft 2D object (typed FeaturePython)
  ChamferSize = 0
  Closed = true
  End = (-69,-50.5,91.5)
  FilletRadius = 0
  Length = 12.5
  MakeFace = true
  Placement = pos=(-56.5,-52.0806,89.7985) rot=(0,0,1;0rad)
  Points = (2) [(0,1.58058,1.7015),(-12.5,1.58058,1.7015)]
  Start = (-56.5,-50.5,91.5)
  Subdivisions = 0
  expr: End.x = -56.5mm - References.LargePlugHeight + References.LargePlugOffset
FEATURE [Part::Sweep] Sweep022
  Frenet = false
  Sections = -> [Circle042]
  Solid = false
  Spine = -> Line012 [Edge1]
  Transition = 1
FEATURE [Part::Part2DObjectPython] Circle044  label="Radi-AGB-Intermediate"  # Draft 2D object (typed FeaturePython)
  FirstAngle = 0
  LastAngle = 0
  MakeFace = true
  Placement = pos=(-69,-50.5,91.5) rot=(0.57735,-0.57735,-0.57735;2.0944rad)
  Radius = 8
  expr: Placement.Base.x = -54mm - References.LargePlugHeight
FEATURE [App::DocumentObjectGroup] Group006  label="Helpers"
  Group = -> [Extrude010,Sweep008,Sweep009,Extrude011,Circle016,Circle017,Line004,Circle018,Circle019,Circle009,Circle024,Sweep,Line,Extrude014,Circle029,Sweep015,Circle030,Circle031,Extrude015,Extrude017,Sweep018,Extrude018,Extrude,Circle042,Circle044,Extrude020,Circle043,Line012]
FEATURE [Part::Sweep] Sweep023
  Frenet = false
  Sections = -> [Circle044]
  Solid = false
  Spine = -> Sketch001005028 [Edge1,Edge2,Edge3]
  Transition = 1
FEATURE [Part::MultiFuse] Fusion044  label="Radi-AGB-Tube"
  Refine = true
  Shapes = -> [Sweep022,Sweep023]
FEATURE [App::DocumentObjectGroup] Group004  label="Tubes"
  Group = -> [Sweep007,Sweep006,Sweep005,Sweep014,Sweep016,Sweep017,Sweep019,Sweep020,Sweep021,Fusion044]
